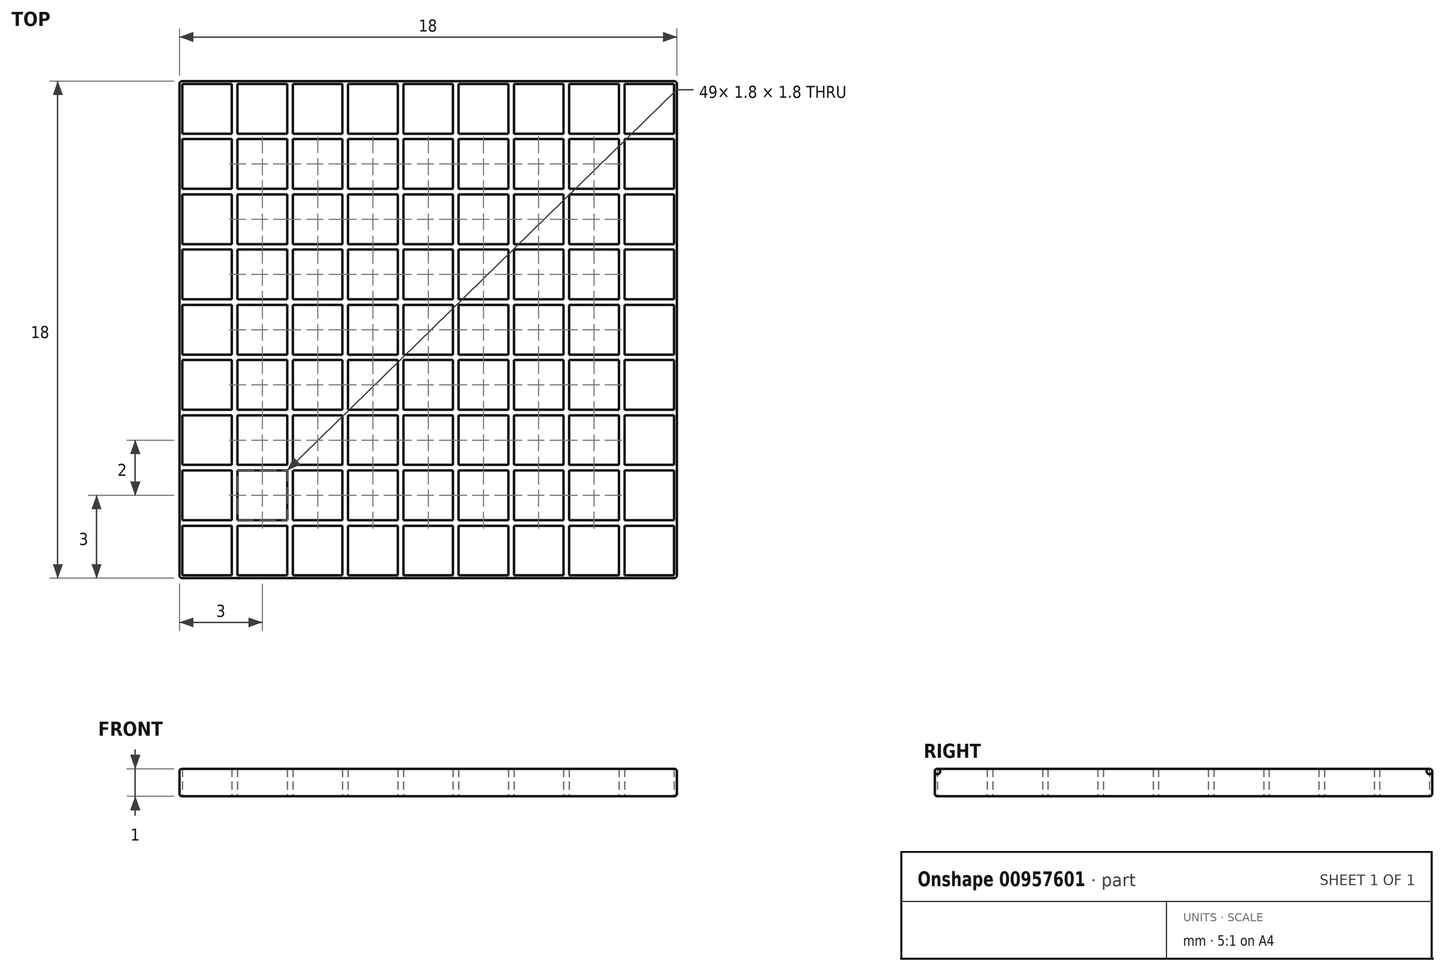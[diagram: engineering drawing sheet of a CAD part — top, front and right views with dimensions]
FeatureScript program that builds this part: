
annotation { "Feature Type Name" : "Feature", "Feature Type Description" : "" }
export const myFeature = defineFeature(function(context is Context, id is Id, definition is map)
    precondition{}
    {
        {
            var Q0;
            Q0=qCreatedBy(makeId("Top.planeOp"),FACE);
            var sketch = newSketch(context, id + "F0", { "sketchPlane" : qUnion([Q0])});
            skLineSegment(sketch, "E0.bottom", {"start": v(-9, 9) * mm, "end": v(9, 9) * mm});
            skLineSegment(sketch, "E0.top", {"start": v(-9, -9) * mm, "end": v(9, -9) * mm});
            skLineSegment(sketch, "E0.left", {"start": v(-9, 9) * mm, "end": v(-9, -9) * mm});
            skLineSegment(sketch, "E0.right", {"start": v(9, 9) * mm, "end": v(9, -9) * mm});
            skPoint(sketch, "E0.middle", {"position": v(0, 0) * mm});
            skLineSegment(sketch, "E1", {"start": v(-8.9, 9) * mm, "end": v(-8.9, -9) * mm});
            skLineSegment(sketch, "E2", {"start": v(-7.1, 9) * mm, "end": v(-7.1, -9) * mm});
            skLineSegment(sketch, "E3", {"start": v(-6.9, 9) * mm, "end": v(-6.9, -9) * mm});
            skLineSegment(sketch, "E4", {"start": v(-5.1, 9) * mm, "end": v(-5.1, -9) * mm});
            skLineSegment(sketch, "E5", {"start": v(-4.9, 9) * mm, "end": v(-4.9, -9) * mm});
            skLineSegment(sketch, "E6", {"start": v(-3.1, 9) * mm, "end": v(-3.1, -9) * mm});
            skLineSegment(sketch, "E7", {"start": v(-2.9, 9) * mm, "end": v(-2.9, -9) * mm});
            skLineSegment(sketch, "E8", {"start": v(-1.1, 9) * mm, "end": v(-1.1, -9) * mm});
            skLineSegment(sketch, "E9", {"start": v(-0.9, 9) * mm, "end": v(-0.9, -9) * mm});
            skLineSegment(sketch, "E10", {"start": v(0.9, 9) * mm, "end": v(0.9, -9) * mm});
            skLineSegment(sketch, "E11", {"start": v(1.1, 9) * mm, "end": v(1.1, -9) * mm});
            skLineSegment(sketch, "E12", {"start": v(2.9, 9) * mm, "end": v(2.9, -9) * mm});
            skLineSegment(sketch, "E13", {"start": v(3.1, 9) * mm, "end": v(3.1, -9) * mm});
            skLineSegment(sketch, "E14", {"start": v(4.9, 9) * mm, "end": v(4.9, -9) * mm});
            skLineSegment(sketch, "E15", {"start": v(5.1, 9) * mm, "end": v(5.1, -9) * mm});
            skLineSegment(sketch, "E16", {"start": v(6.9, 9) * mm, "end": v(6.9, -9) * mm});
            skLineSegment(sketch, "E17", {"start": v(7.1, 9) * mm, "end": v(7.1, -9) * mm});
            skLineSegment(sketch, "E18", {"start": v(8.9, 9) * mm, "end": v(8.9, -9) * mm});
            skLineSegment(sketch, "E19", {"start": v(9, 8.9) * mm, "end": v(-9, 8.9) * mm});
            skLineSegment(sketch, "E20", {"start": v(9, 7.1) * mm, "end": v(-9, 7.1) * mm});
            skLineSegment(sketch, "E21", {"start": v(9, 6.9) * mm, "end": v(-9, 6.9) * mm});
            skLineSegment(sketch, "E22", {"start": v(9, 5.1) * mm, "end": v(-9, 5.1) * mm});
            skLineSegment(sketch, "E23", {"start": v(9, 4.9) * mm, "end": v(-9, 4.9) * mm});
            skLineSegment(sketch, "E24", {"start": v(9, 3.1) * mm, "end": v(-9, 3.1) * mm});
            skLineSegment(sketch, "E25", {"start": v(9, 2.9) * mm, "end": v(-9, 2.9) * mm});
            skLineSegment(sketch, "E26", {"start": v(9, 1.1) * mm, "end": v(-9, 1.1) * mm});
            skLineSegment(sketch, "E27", {"start": v(9, 0.9) * mm, "end": v(-9, 0.9) * mm});
            skLineSegment(sketch, "E28", {"start": v(9, -0.9) * mm, "end": v(-9, -0.9) * mm});
            skLineSegment(sketch, "E29", {"start": v(9, -1.1) * mm, "end": v(-9, -1.1) * mm});
            skLineSegment(sketch, "E30", {"start": v(9, -2.9) * mm, "end": v(-9, -2.9) * mm});
            skLineSegment(sketch, "E31", {"start": v(9, -3.1) * mm, "end": v(-9, -3.1) * mm});
            skLineSegment(sketch, "E32", {"start": v(9, -4.9) * mm, "end": v(-9, -4.9) * mm});
            skLineSegment(sketch, "E33", {"start": v(9, -5.1) * mm, "end": v(-9, -5.1) * mm});
            skLineSegment(sketch, "E34", {"start": v(9, -6.9) * mm, "end": v(-9, -6.9) * mm});
            skLineSegment(sketch, "E35", {"start": v(9, -7.1) * mm, "end": v(-9, -7.1) * mm});
            skLineSegment(sketch, "E36", {"start": v(9, -8.9) * mm, "end": v(-9, -8.9) * mm});
            skSolve(sketch);
        }
        {
            var Q0;
            {var subQ0=sQuery(id+"F0.wireOp",EDGE,"E30");var subQ1=sQuery(id+"F0.wireOp",EDGE,"E10");var subQ2=makeQuery(id+"F0.imprint","INTERSECT",VERTEX,{"derivedFrom":[subQ1,subQ0]});Q0=makeQuery(id+"F0.imprint","IMPRINT",FACE,{"disambiguationData":[TD([[makeQuery(id+"F0.imprint","IMPRINT",EDGE,{"disambiguationData":[TD([[subQ2,-1.0]])],"derivedFrom":subQ1}),1.0]])]});}
            var Q1;
            {var subQ0=sQuery(id+"F0.wireOp",EDGE,"E26");var subQ1=sQuery(id+"F0.wireOp",EDGE,"E11");var subQ2=makeQuery(id+"F0.imprint","INTERSECT",VERTEX,{"derivedFrom":[subQ1,subQ0]});Q1=makeQuery(id+"F0.imprint","IMPRINT",FACE,{"disambiguationData":[TD([[makeQuery(id+"F0.imprint","IMPRINT",EDGE,{"disambiguationData":[TD([[subQ2,-1.0]])],"derivedFrom":subQ1}),1.0]])]});}
            var Q2;
            {var subQ0=sQuery(id+"F0.wireOp",EDGE,"E25");var subQ1=sQuery(id+"F0.wireOp",EDGE,"E8");var subQ2=makeQuery(id+"F0.imprint","INTERSECT",VERTEX,{"derivedFrom":[subQ1,subQ0]});Q2=makeQuery(id+"F0.imprint","IMPRINT",FACE,{"disambiguationData":[TD([[makeQuery(id+"F0.imprint","IMPRINT",EDGE,{"disambiguationData":[TD([[subQ2,-1.0]])],"derivedFrom":subQ1}),1.0]])]});}
            var Q3;
            {var subQ0=sQuery(id+"F0.wireOp",EDGE,"E24");var subQ1=sQuery(id+"F0.wireOp",EDGE,"E10");var subQ2=makeQuery(id+"F0.imprint","INTERSECT",VERTEX,{"derivedFrom":[subQ1,subQ0]});Q3=makeQuery(id+"F0.imprint","IMPRINT",FACE,{"disambiguationData":[TD([[makeQuery(id+"F0.imprint","IMPRINT",EDGE,{"disambiguationData":[TD([[subQ2,-1.0]])],"derivedFrom":subQ1}),1.0]])]});}
            var Q4;
            {var subQ0=sQuery(id+"F0.wireOp",EDGE,"E30");var subQ1=sQuery(id+"F0.wireOp",EDGE,"E15");var subQ2=makeQuery(id+"F0.imprint","INTERSECT",VERTEX,{"derivedFrom":[subQ1,subQ0]});Q4=makeQuery(id+"F0.imprint","IMPRINT",FACE,{"disambiguationData":[TD([[makeQuery(id+"F0.imprint","IMPRINT",EDGE,{"disambiguationData":[TD([[subQ2,-1.0]])],"derivedFrom":subQ1}),1.0]])]});}
            var Q5;
            {var subQ0=sQuery(id+"F0.wireOp",EDGE,"E35");var subQ1=sQuery(id+"F0.wireOp",EDGE,"E12");var subQ2=makeQuery(id+"F0.imprint","INTERSECT",VERTEX,{"derivedFrom":[subQ1,subQ0]});Q5=makeQuery(id+"F0.imprint","IMPRINT",FACE,{"disambiguationData":[TD([[makeQuery(id+"F0.imprint","IMPRINT",EDGE,{"disambiguationData":[TD([[subQ2,-1.0]])],"derivedFrom":subQ1}),1.0]])]});}
            var Q6;
            {var subQ0=sQuery(id+"F0.wireOp",EDGE,"E35");var subQ1=sQuery(id+"F0.wireOp",EDGE,"E14");var subQ2=makeQuery(id+"F0.imprint","INTERSECT",VERTEX,{"derivedFrom":[subQ1,subQ0]});Q6=makeQuery(id+"F0.imprint","IMPRINT",FACE,{"disambiguationData":[TD([[makeQuery(id+"F0.imprint","IMPRINT",EDGE,{"disambiguationData":[TD([[subQ2,-1.0]])],"derivedFrom":subQ1}),1.0]])]});}
            var Q7;
            {var subQ0=sQuery(id+"F0.wireOp",EDGE,"E32");var subQ1=sQuery(id+"F0.wireOp",EDGE,"E10");var subQ2=makeQuery(id+"F0.imprint","INTERSECT",VERTEX,{"derivedFrom":[subQ1,subQ0]});Q7=makeQuery(id+"F0.imprint","IMPRINT",FACE,{"disambiguationData":[TD([[makeQuery(id+"F0.imprint","IMPRINT",EDGE,{"disambiguationData":[TD([[subQ2,-1.0]])],"derivedFrom":subQ1}),1.0]])]});}
            var Q8;
            {var subQ0=sQuery(id+"F0.wireOp",EDGE,"E23");var subQ1=sQuery(id+"F0.wireOp",EDGE,"E14");var subQ2=makeQuery(id+"F0.imprint","INTERSECT",VERTEX,{"derivedFrom":[subQ1,subQ0]});Q8=makeQuery(id+"F0.imprint","IMPRINT",FACE,{"disambiguationData":[TD([[makeQuery(id+"F0.imprint","IMPRINT",EDGE,{"disambiguationData":[TD([[subQ2,-1.0]])],"derivedFrom":subQ1}),1.0]])]});}
            var Q9;
            {var subQ0=sQuery(id+"F0.wireOp",EDGE,"E23");var subQ1=sQuery(id+"F0.wireOp",EDGE,"E16");var subQ2=makeQuery(id+"F0.imprint","INTERSECT",VERTEX,{"derivedFrom":[subQ1,subQ0]});Q9=makeQuery(id+"F0.imprint","IMPRINT",FACE,{"disambiguationData":[TD([[makeQuery(id+"F0.imprint","IMPRINT",EDGE,{"disambiguationData":[TD([[subQ2,-1.0]])],"derivedFrom":subQ1}),1.0]])]});}
            var Q10;
            {var subQ0=sQuery(id+"F0.wireOp",EDGE,"E22");var subQ1=sQuery(id+"F0.wireOp",EDGE,"E9");var subQ2=makeQuery(id+"F0.imprint","INTERSECT",VERTEX,{"derivedFrom":[subQ1,subQ0]});Q10=makeQuery(id+"F0.imprint","IMPRINT",FACE,{"disambiguationData":[TD([[makeQuery(id+"F0.imprint","IMPRINT",EDGE,{"disambiguationData":[TD([[subQ2,-1.0]])],"derivedFrom":subQ1}),1.0]])]});}
            var Q11;
            {var subQ0=sQuery(id+"F0.wireOp",EDGE,"E27");var subQ1=sQuery(id+"F0.wireOp",EDGE,"E10");var subQ2=makeQuery(id+"F0.imprint","INTERSECT",VERTEX,{"derivedFrom":[subQ1,subQ0]});Q11=makeQuery(id+"F0.imprint","IMPRINT",FACE,{"disambiguationData":[TD([[makeQuery(id+"F0.imprint","IMPRINT",EDGE,{"disambiguationData":[TD([[subQ2,-1.0]])],"derivedFrom":subQ1}),1.0]])]});}
            var Q12;
            {var subQ0=sQuery(id+"F0.wireOp",EDGE,"E31");var subQ1=sQuery(id+"F0.wireOp",EDGE,"E2");var subQ2=makeQuery(id+"F0.imprint","INTERSECT",VERTEX,{"derivedFrom":[subQ1,subQ0]});Q12=makeQuery(id+"F0.imprint","IMPRINT",FACE,{"disambiguationData":[TD([[makeQuery(id+"F0.imprint","IMPRINT",EDGE,{"disambiguationData":[TD([[subQ2,-1.0]])],"derivedFrom":subQ1}),1.0]])]});}
            var Q13;
            {var subQ0=sQuery(id+"F0.wireOp",EDGE,"E30");var subQ1=sQuery(id+"F0.wireOp",EDGE,"E13");var subQ2=makeQuery(id+"F0.imprint","INTERSECT",VERTEX,{"derivedFrom":[subQ1,subQ0]});Q13=makeQuery(id+"F0.imprint","IMPRINT",FACE,{"disambiguationData":[TD([[makeQuery(id+"F0.imprint","IMPRINT",EDGE,{"disambiguationData":[TD([[subQ2,-1.0]])],"derivedFrom":subQ1}),1.0]])]});}
            var Q14;
            {var subQ0=sQuery(id+"F0.wireOp",EDGE,"E33");var subQ1=sQuery(id+"F0.wireOp",EDGE,"E16");var subQ2=makeQuery(id+"F0.imprint","INTERSECT",VERTEX,{"derivedFrom":[subQ1,subQ0]});Q14=makeQuery(id+"F0.imprint","IMPRINT",FACE,{"disambiguationData":[TD([[makeQuery(id+"F0.imprint","IMPRINT",EDGE,{"disambiguationData":[TD([[subQ2,-1.0]])],"derivedFrom":subQ1}),1.0]])]});}
            var Q15;
            {var subQ0=sQuery(id+"F0.wireOp",EDGE,"E29");var subQ1=sQuery(id+"F0.wireOp",EDGE,"E8");var subQ2=makeQuery(id+"F0.imprint","INTERSECT",VERTEX,{"derivedFrom":[subQ1,subQ0]});Q15=makeQuery(id+"F0.imprint","IMPRINT",FACE,{"disambiguationData":[TD([[makeQuery(id+"F0.imprint","IMPRINT",EDGE,{"disambiguationData":[TD([[subQ2,-1.0]])],"derivedFrom":subQ1}),1.0]])]});}
            var Q16;
            {var subQ0=sQuery(id+"F0.wireOp",EDGE,"E26");var subQ1=sQuery(id+"F0.wireOp",EDGE,"E1");var subQ2=makeQuery(id+"F0.imprint","INTERSECT",VERTEX,{"derivedFrom":[subQ1,subQ0]});Q16=makeQuery(id+"F0.imprint","IMPRINT",FACE,{"disambiguationData":[TD([[makeQuery(id+"F0.imprint","IMPRINT",EDGE,{"disambiguationData":[TD([[subQ2,-1.0]])],"derivedFrom":subQ1}),1.0]])]});}
            var Q17;
            {var subQ0=sQuery(id+"F0.wireOp",EDGE,"E30");var subQ1=sQuery(id+"F0.wireOp",EDGE,"E12");var subQ2=makeQuery(id+"F0.imprint","INTERSECT",VERTEX,{"derivedFrom":[subQ1,subQ0]});Q17=makeQuery(id+"F0.imprint","IMPRINT",FACE,{"disambiguationData":[TD([[makeQuery(id+"F0.imprint","IMPRINT",EDGE,{"disambiguationData":[TD([[subQ2,-1.0]])],"derivedFrom":subQ1}),1.0]])]});}
            var Q18;
            {var subQ0=sQuery(id+"F0.wireOp",EDGE,"E29");var subQ1=sQuery(id+"F0.wireOp",EDGE,"E12");var subQ2=makeQuery(id+"F0.imprint","INTERSECT",VERTEX,{"derivedFrom":[subQ1,subQ0]});Q18=makeQuery(id+"F0.imprint","IMPRINT",FACE,{"disambiguationData":[TD([[makeQuery(id+"F0.imprint","IMPRINT",EDGE,{"disambiguationData":[TD([[subQ2,-1.0]])],"derivedFrom":subQ1}),1.0]])]});}
            var Q19;
            {var subQ0=sQuery(id+"F0.wireOp",EDGE,"E31");var subQ1=sQuery(id+"F0.wireOp",EDGE,"E6");var subQ2=makeQuery(id+"F0.imprint","INTERSECT",VERTEX,{"derivedFrom":[subQ1,subQ0]});Q19=makeQuery(id+"F0.imprint","IMPRINT",FACE,{"disambiguationData":[TD([[makeQuery(id+"F0.imprint","IMPRINT",EDGE,{"disambiguationData":[TD([[subQ2,-1.0]])],"derivedFrom":subQ1}),1.0]])]});}
            var Q20;
            {var subQ0=sQuery(id+"F0.wireOp",EDGE,"E29");var subQ1=sQuery(id+"F0.wireOp",EDGE,"E10");var subQ2=makeQuery(id+"F0.imprint","INTERSECT",VERTEX,{"derivedFrom":[subQ1,subQ0]});Q20=makeQuery(id+"F0.imprint","IMPRINT",FACE,{"disambiguationData":[TD([[makeQuery(id+"F0.imprint","IMPRINT",EDGE,{"disambiguationData":[TD([[subQ2,-1.0]])],"derivedFrom":subQ1}),1.0]])]});}
            var Q21;
            {var subQ0=sQuery(id+"F0.wireOp",EDGE,"E25");var subQ1=sQuery(id+"F0.wireOp",EDGE,"E16");var subQ2=makeQuery(id+"F0.imprint","INTERSECT",VERTEX,{"derivedFrom":[subQ1,subQ0]});Q21=makeQuery(id+"F0.imprint","IMPRINT",FACE,{"disambiguationData":[TD([[makeQuery(id+"F0.imprint","IMPRINT",EDGE,{"disambiguationData":[TD([[subQ2,-1.0]])],"derivedFrom":subQ1}),1.0]])]});}
            var Q22;
            {var subQ0=sQuery(id+"F0.wireOp",EDGE,"E35");var subQ1=sQuery(id+"F0.wireOp",EDGE,"E16");var subQ2=makeQuery(id+"F0.imprint","INTERSECT",VERTEX,{"derivedFrom":[subQ1,subQ0]});Q22=makeQuery(id+"F0.imprint","IMPRINT",FACE,{"disambiguationData":[TD([[makeQuery(id+"F0.imprint","IMPRINT",EDGE,{"disambiguationData":[TD([[subQ2,-1.0]])],"derivedFrom":subQ1}),1.0]])]});}
            var Q23;
            {var subQ0=sQuery(id+"F0.wireOp",EDGE,"E31");var subQ1=sQuery(id+"F0.wireOp",EDGE,"E12");var subQ2=makeQuery(id+"F0.imprint","INTERSECT",VERTEX,{"derivedFrom":[subQ1,subQ0]});Q23=makeQuery(id+"F0.imprint","IMPRINT",FACE,{"disambiguationData":[TD([[makeQuery(id+"F0.imprint","IMPRINT",EDGE,{"disambiguationData":[TD([[subQ2,-1.0]])],"derivedFrom":subQ1}),1.0]])]});}
            var Q24;
            {var subQ0=sQuery(id+"F0.wireOp",EDGE,"E24");var subQ1=sQuery(id+"F0.wireOp",EDGE,"E1");var subQ2=makeQuery(id+"F0.imprint","INTERSECT",VERTEX,{"derivedFrom":[subQ1,subQ0]});Q24=makeQuery(id+"F0.imprint","IMPRINT",FACE,{"disambiguationData":[TD([[makeQuery(id+"F0.imprint","IMPRINT",EDGE,{"disambiguationData":[TD([[subQ2,-1.0]])],"derivedFrom":subQ1}),1.0]])]});}
            var Q25;
            {var subQ0=sQuery(id+"F0.wireOp",EDGE,"E27");var subQ1=sQuery(id+"F0.wireOp",EDGE,"E16");var subQ2=makeQuery(id+"F0.imprint","INTERSECT",VERTEX,{"derivedFrom":[subQ1,subQ0]});Q25=makeQuery(id+"F0.imprint","IMPRINT",FACE,{"disambiguationData":[TD([[makeQuery(id+"F0.imprint","IMPRINT",EDGE,{"disambiguationData":[TD([[subQ2,-1.0]])],"derivedFrom":subQ1}),1.0]])]});}
            var Q26;
            {var subQ0=sQuery(id+"F0.wireOp",EDGE,"E26");var subQ1=sQuery(id+"F0.wireOp",EDGE,"E9");var subQ2=makeQuery(id+"F0.imprint","INTERSECT",VERTEX,{"derivedFrom":[subQ1,subQ0]});Q26=makeQuery(id+"F0.imprint","IMPRINT",FACE,{"disambiguationData":[TD([[makeQuery(id+"F0.imprint","IMPRINT",EDGE,{"disambiguationData":[TD([[subQ2,-1.0]])],"derivedFrom":subQ1}),1.0]])]});}
            var Q27;
            {var subQ0=sQuery(id+"F0.wireOp",EDGE,"E35");var subQ1=sQuery(id+"F0.wireOp",EDGE,"E2");var subQ2=makeQuery(id+"F0.imprint","INTERSECT",VERTEX,{"derivedFrom":[subQ1,subQ0]});Q27=makeQuery(id+"F0.imprint","IMPRINT",FACE,{"disambiguationData":[TD([[makeQuery(id+"F0.imprint","IMPRINT",EDGE,{"disambiguationData":[TD([[subQ2,-1.0]])],"derivedFrom":subQ1}),1.0]])]});}
            var Q28;
            {var subQ0=sQuery(id+"F0.wireOp",EDGE,"E22");var subQ1=sQuery(id+"F0.wireOp",EDGE,"E16");var subQ2=makeQuery(id+"F0.imprint","INTERSECT",VERTEX,{"derivedFrom":[subQ1,subQ0]});Q28=makeQuery(id+"F0.imprint","IMPRINT",FACE,{"disambiguationData":[TD([[makeQuery(id+"F0.imprint","IMPRINT",EDGE,{"disambiguationData":[TD([[subQ2,-1.0]])],"derivedFrom":subQ1}),1.0]])]});}
            var Q29;
            {var subQ0=sQuery(id+"F0.wireOp",EDGE,"E35");var subQ1=sQuery(id+"F0.wireOp",EDGE,"E8");var subQ2=makeQuery(id+"F0.imprint","INTERSECT",VERTEX,{"derivedFrom":[subQ1,subQ0]});Q29=makeQuery(id+"F0.imprint","IMPRINT",FACE,{"disambiguationData":[TD([[makeQuery(id+"F0.imprint","IMPRINT",EDGE,{"disambiguationData":[TD([[subQ2,-1.0]])],"derivedFrom":subQ1}),1.0]])]});}
            var Q30;
            {var subQ0=sQuery(id+"F0.wireOp",EDGE,"E24");var subQ1=sQuery(id+"F0.wireOp",EDGE,"E7");var subQ2=makeQuery(id+"F0.imprint","INTERSECT",VERTEX,{"derivedFrom":[subQ1,subQ0]});Q30=makeQuery(id+"F0.imprint","IMPRINT",FACE,{"disambiguationData":[TD([[makeQuery(id+"F0.imprint","IMPRINT",EDGE,{"disambiguationData":[TD([[subQ2,-1.0]])],"derivedFrom":subQ1}),1.0]])]});}
            var Q31;
            {var subQ0=sQuery(id+"F0.wireOp",EDGE,"E21");var subQ1=sQuery(id+"F0.wireOp",EDGE,"E16");var subQ2=makeQuery(id+"F0.imprint","INTERSECT",VERTEX,{"derivedFrom":[subQ1,subQ0]});Q31=makeQuery(id+"F0.imprint","IMPRINT",FACE,{"disambiguationData":[TD([[makeQuery(id+"F0.imprint","IMPRINT",EDGE,{"disambiguationData":[TD([[subQ2,-1.0]])],"derivedFrom":subQ1}),1.0]])]});}
            var Q32;
            {var subQ0=sQuery(id+"F0.wireOp",EDGE,"E32");var subQ1=sQuery(id+"F0.wireOp",EDGE,"E11");var subQ2=makeQuery(id+"F0.imprint","INTERSECT",VERTEX,{"derivedFrom":[subQ1,subQ0]});Q32=makeQuery(id+"F0.imprint","IMPRINT",FACE,{"disambiguationData":[TD([[makeQuery(id+"F0.imprint","IMPRINT",EDGE,{"disambiguationData":[TD([[subQ2,-1.0]])],"derivedFrom":subQ1}),1.0]])]});}
            var Q33;
            {var subQ0=sQuery(id+"F0.wireOp",EDGE,"E33");var subQ1=sQuery(id+"F0.wireOp",EDGE,"E8");var subQ2=makeQuery(id+"F0.imprint","INTERSECT",VERTEX,{"derivedFrom":[subQ1,subQ0]});Q33=makeQuery(id+"F0.imprint","IMPRINT",FACE,{"disambiguationData":[TD([[makeQuery(id+"F0.imprint","IMPRINT",EDGE,{"disambiguationData":[TD([[subQ2,-1.0]])],"derivedFrom":subQ1}),1.0]])]});}
            var Q34;
            {var subQ0=sQuery(id+"F0.wireOp",EDGE,"E30");var subQ1=sQuery(id+"F0.wireOp",EDGE,"E9");var subQ2=makeQuery(id+"F0.imprint","INTERSECT",VERTEX,{"derivedFrom":[subQ1,subQ0]});Q34=makeQuery(id+"F0.imprint","IMPRINT",FACE,{"disambiguationData":[TD([[makeQuery(id+"F0.imprint","IMPRINT",EDGE,{"disambiguationData":[TD([[subQ2,-1.0]])],"derivedFrom":subQ1}),1.0]])]});}
            var Q35;
            {var subQ0=sQuery(id+"F0.wireOp",EDGE,"E22");var subQ1=sQuery(id+"F0.wireOp",EDGE,"E8");var subQ2=makeQuery(id+"F0.imprint","INTERSECT",VERTEX,{"derivedFrom":[subQ1,subQ0]});Q35=makeQuery(id+"F0.imprint","IMPRINT",FACE,{"disambiguationData":[TD([[makeQuery(id+"F0.imprint","IMPRINT",EDGE,{"disambiguationData":[TD([[subQ2,-1.0]])],"derivedFrom":subQ1}),1.0]])]});}
            var Q36;
            {var subQ0=sQuery(id+"F0.wireOp",EDGE,"E27");var subQ1=sQuery(id+"F0.wireOp",EDGE,"E2");var subQ2=makeQuery(id+"F0.imprint","INTERSECT",VERTEX,{"derivedFrom":[subQ1,subQ0]});Q36=makeQuery(id+"F0.imprint","IMPRINT",FACE,{"disambiguationData":[TD([[makeQuery(id+"F0.imprint","IMPRINT",EDGE,{"disambiguationData":[TD([[subQ2,-1.0]])],"derivedFrom":subQ1}),1.0]])]});}
            var Q37;
            {var subQ0=sQuery(id+"F0.wireOp",EDGE,"E30");var subQ1=sQuery(id+"F0.wireOp",EDGE,"E11");var subQ2=makeQuery(id+"F0.imprint","INTERSECT",VERTEX,{"derivedFrom":[subQ1,subQ0]});Q37=makeQuery(id+"F0.imprint","IMPRINT",FACE,{"disambiguationData":[TD([[makeQuery(id+"F0.imprint","IMPRINT",EDGE,{"disambiguationData":[TD([[subQ2,-1.0]])],"derivedFrom":subQ1}),1.0]])]});}
            var Q38;
            {var subQ0=sQuery(id+"F0.wireOp",EDGE,"E26");var subQ1=sQuery(id+"F0.wireOp",EDGE,"E5");var subQ2=makeQuery(id+"F0.imprint","INTERSECT",VERTEX,{"derivedFrom":[subQ1,subQ0]});Q38=makeQuery(id+"F0.imprint","IMPRINT",FACE,{"disambiguationData":[TD([[makeQuery(id+"F0.imprint","IMPRINT",EDGE,{"disambiguationData":[TD([[subQ2,-1.0]])],"derivedFrom":subQ1}),1.0]])]});}
            var Q39;
            {var subQ0=sQuery(id+"F0.wireOp",EDGE,"E31");var subQ1=sQuery(id+"F0.wireOp",EDGE,"E8");var subQ2=makeQuery(id+"F0.imprint","INTERSECT",VERTEX,{"derivedFrom":[subQ1,subQ0]});Q39=makeQuery(id+"F0.imprint","IMPRINT",FACE,{"disambiguationData":[TD([[makeQuery(id+"F0.imprint","IMPRINT",EDGE,{"disambiguationData":[TD([[subQ2,-1.0]])],"derivedFrom":subQ1}),1.0]])]});}
            var Q40;
            {var subQ0=sQuery(id+"F0.wireOp",EDGE,"E32");var subQ1=sQuery(id+"F0.wireOp",EDGE,"E7");var subQ2=makeQuery(id+"F0.imprint","INTERSECT",VERTEX,{"derivedFrom":[subQ1,subQ0]});Q40=makeQuery(id+"F0.imprint","IMPRINT",FACE,{"disambiguationData":[TD([[makeQuery(id+"F0.imprint","IMPRINT",EDGE,{"disambiguationData":[TD([[subQ2,-1.0]])],"derivedFrom":subQ1}),1.0]])]});}
            var Q41;
            {var subQ0=sQuery(id+"F0.wireOp",EDGE,"E24");var subQ1=sQuery(id+"F0.wireOp",EDGE,"E17");var subQ2=makeQuery(id+"F0.imprint","INTERSECT",VERTEX,{"derivedFrom":[subQ1,subQ0]});Q41=makeQuery(id+"F0.imprint","IMPRINT",FACE,{"disambiguationData":[TD([[makeQuery(id+"F0.imprint","IMPRINT",EDGE,{"disambiguationData":[TD([[subQ2,-1.0]])],"derivedFrom":subQ1}),1.0]])]});}
            var Q42;
            {var subQ0=sQuery(id+"F0.wireOp",EDGE,"E26");var subQ1=sQuery(id+"F0.wireOp",EDGE,"E14");var subQ2=makeQuery(id+"F0.imprint","INTERSECT",VERTEX,{"derivedFrom":[subQ1,subQ0]});Q42=makeQuery(id+"F0.imprint","IMPRINT",FACE,{"disambiguationData":[TD([[makeQuery(id+"F0.imprint","IMPRINT",EDGE,{"disambiguationData":[TD([[subQ2,-1.0]])],"derivedFrom":subQ1}),1.0]])]});}
            var Q43;
            {var subQ0=sQuery(id+"F0.wireOp",EDGE,"E31");var subQ1=sQuery(id+"F0.wireOp",EDGE,"E14");var subQ2=makeQuery(id+"F0.imprint","INTERSECT",VERTEX,{"derivedFrom":[subQ1,subQ0]});Q43=makeQuery(id+"F0.imprint","IMPRINT",FACE,{"disambiguationData":[TD([[makeQuery(id+"F0.imprint","IMPRINT",EDGE,{"disambiguationData":[TD([[subQ2,-1.0]])],"derivedFrom":subQ1}),1.0]])]});}
            var Q44;
            {var subQ0=sQuery(id+"F0.wireOp",EDGE,"E24");var subQ1=sQuery(id+"F0.wireOp",EDGE,"E5");var subQ2=makeQuery(id+"F0.imprint","INTERSECT",VERTEX,{"derivedFrom":[subQ1,subQ0]});Q44=makeQuery(id+"F0.imprint","IMPRINT",FACE,{"disambiguationData":[TD([[makeQuery(id+"F0.imprint","IMPRINT",EDGE,{"disambiguationData":[TD([[subQ2,-1.0]])],"derivedFrom":subQ1}),1.0]])]});}
            var Q45;
            {var subQ0=sQuery(id+"F0.wireOp",EDGE,"E26");var subQ1=sQuery(id+"F0.wireOp",EDGE,"E12");var subQ2=makeQuery(id+"F0.imprint","INTERSECT",VERTEX,{"derivedFrom":[subQ1,subQ0]});Q45=makeQuery(id+"F0.imprint","IMPRINT",FACE,{"disambiguationData":[TD([[makeQuery(id+"F0.imprint","IMPRINT",EDGE,{"disambiguationData":[TD([[subQ2,-1.0]])],"derivedFrom":subQ1}),1.0]])]});}
            var Q46;
            {var subQ0=sQuery(id+"F0.wireOp",EDGE,"E30");var subQ1=sQuery(id+"F0.wireOp",EDGE,"E5");var subQ2=makeQuery(id+"F0.imprint","INTERSECT",VERTEX,{"derivedFrom":[subQ1,subQ0]});Q46=makeQuery(id+"F0.imprint","IMPRINT",FACE,{"disambiguationData":[TD([[makeQuery(id+"F0.imprint","IMPRINT",EDGE,{"disambiguationData":[TD([[subQ2,-1.0]])],"derivedFrom":subQ1}),1.0]])]});}
            var Q47;
            {var subQ0=sQuery(id+"F0.wireOp",EDGE,"E33");var subQ1=sQuery(id+"F0.wireOp",EDGE,"E14");var subQ2=makeQuery(id+"F0.imprint","INTERSECT",VERTEX,{"derivedFrom":[subQ1,subQ0]});Q47=makeQuery(id+"F0.imprint","IMPRINT",FACE,{"disambiguationData":[TD([[makeQuery(id+"F0.imprint","IMPRINT",EDGE,{"disambiguationData":[TD([[subQ2,-1.0]])],"derivedFrom":subQ1}),1.0]])]});}
            var Q48;
            {var subQ0=sQuery(id+"F0.wireOp",EDGE,"E32");var subQ1=sQuery(id+"F0.wireOp",EDGE,"E9");var subQ2=makeQuery(id+"F0.imprint","INTERSECT",VERTEX,{"derivedFrom":[subQ1,subQ0]});Q48=makeQuery(id+"F0.imprint","IMPRINT",FACE,{"disambiguationData":[TD([[makeQuery(id+"F0.imprint","IMPRINT",EDGE,{"disambiguationData":[TD([[subQ2,-1.0]])],"derivedFrom":subQ1}),1.0]])]});}
            var Q49;
            {var subQ0=sQuery(id+"F0.wireOp",EDGE,"E25");var subQ1=sQuery(id+"F0.wireOp",EDGE,"E6");var subQ2=makeQuery(id+"F0.imprint","INTERSECT",VERTEX,{"derivedFrom":[subQ1,subQ0]});Q49=makeQuery(id+"F0.imprint","IMPRINT",FACE,{"disambiguationData":[TD([[makeQuery(id+"F0.imprint","IMPRINT",EDGE,{"disambiguationData":[TD([[subQ2,-1.0]])],"derivedFrom":subQ1}),1.0]])]});}
            var Q50;
            {var subQ0=sQuery(id+"F0.wireOp",EDGE,"E19");var subQ1=sQuery(id+"F0.wireOp",EDGE,"E16");var subQ2=makeQuery(id+"F0.imprint","INTERSECT",VERTEX,{"derivedFrom":[subQ1,subQ0]});Q50=makeQuery(id+"F0.imprint","IMPRINT",FACE,{"disambiguationData":[TD([[makeQuery(id+"F0.imprint","IMPRINT",EDGE,{"disambiguationData":[TD([[subQ2,-1.0]])],"derivedFrom":subQ1}),1.0]])]});}
            var Q51;
            {var subQ0=sQuery(id+"F0.wireOp",EDGE,"E19");var subQ1=sQuery(id+"F0.wireOp",EDGE,"E10");var subQ2=makeQuery(id+"F0.imprint","INTERSECT",VERTEX,{"derivedFrom":[subQ1,subQ0]});Q51=makeQuery(id+"F0.imprint","IMPRINT",FACE,{"disambiguationData":[TD([[makeQuery(id+"F0.imprint","IMPRINT",EDGE,{"disambiguationData":[TD([[subQ2,-1.0]])],"derivedFrom":subQ1}),1.0]])]});}
            var Q52;
            {var subQ0=sQuery(id+"F0.wireOp",EDGE,"E19");var subQ1=sQuery(id+"F0.wireOp",EDGE,"E2");var subQ2=makeQuery(id+"F0.imprint","INTERSECT",VERTEX,{"derivedFrom":[subQ1,subQ0]});Q52=makeQuery(id+"F0.imprint","IMPRINT",FACE,{"disambiguationData":[TD([[makeQuery(id+"F0.imprint","IMPRINT",EDGE,{"disambiguationData":[TD([[subQ2,-1.0]])],"derivedFrom":subQ1}),1.0]])]});}
            var Q53;
            {var subQ0=sQuery(id+"F0.wireOp",EDGE,"E32");var subQ1=sQuery(id+"F0.wireOp",EDGE,"E17");var subQ2=makeQuery(id+"F0.imprint","INTERSECT",VERTEX,{"derivedFrom":[subQ1,subQ0]});Q53=makeQuery(id+"F0.imprint","IMPRINT",FACE,{"disambiguationData":[TD([[makeQuery(id+"F0.imprint","IMPRINT",EDGE,{"disambiguationData":[TD([[subQ2,-1.0]])],"derivedFrom":subQ1}),1.0]])]});}
            var Q54;
            {var subQ0=sQuery(id+"F0.wireOp",EDGE,"E30");var subQ1=sQuery(id+"F0.wireOp",EDGE,"E17");var subQ2=makeQuery(id+"F0.imprint","INTERSECT",VERTEX,{"derivedFrom":[subQ1,subQ0]});Q54=makeQuery(id+"F0.imprint","IMPRINT",FACE,{"disambiguationData":[TD([[makeQuery(id+"F0.imprint","IMPRINT",EDGE,{"disambiguationData":[TD([[subQ2,-1.0]])],"derivedFrom":subQ1}),1.0]])]});}
            var Q55;
            {var subQ0=sQuery(id+"F0.wireOp",EDGE,"E33");var subQ1=sQuery(id+"F0.wireOp",EDGE,"E12");var subQ2=makeQuery(id+"F0.imprint","INTERSECT",VERTEX,{"derivedFrom":[subQ1,subQ0]});Q55=makeQuery(id+"F0.imprint","IMPRINT",FACE,{"disambiguationData":[TD([[makeQuery(id+"F0.imprint","IMPRINT",EDGE,{"disambiguationData":[TD([[subQ2,-1.0]])],"derivedFrom":subQ1}),1.0]])]});}
            var Q56;
            {var subQ0=sQuery(id+"F0.wireOp",EDGE,"E24");var subQ1=sQuery(id+"F0.wireOp",EDGE,"E8");var subQ2=makeQuery(id+"F0.imprint","INTERSECT",VERTEX,{"derivedFrom":[subQ1,subQ0]});Q56=makeQuery(id+"F0.imprint","IMPRINT",FACE,{"disambiguationData":[TD([[makeQuery(id+"F0.imprint","IMPRINT",EDGE,{"disambiguationData":[TD([[subQ2,-1.0]])],"derivedFrom":subQ1}),1.0]])]});}
            var Q57;
            {var subQ0=sQuery(id+"F0.wireOp",EDGE,"E22");var subQ1=sQuery(id+"F0.wireOp",EDGE,"E13");var subQ2=makeQuery(id+"F0.imprint","INTERSECT",VERTEX,{"derivedFrom":[subQ1,subQ0]});Q57=makeQuery(id+"F0.imprint","IMPRINT",FACE,{"disambiguationData":[TD([[makeQuery(id+"F0.imprint","IMPRINT",EDGE,{"disambiguationData":[TD([[subQ2,-1.0]])],"derivedFrom":subQ1}),1.0]])]});}
            var Q58;
            {var subQ0=sQuery(id+"F0.wireOp",EDGE,"E19");var subQ1=sQuery(id+"F0.wireOp",EDGE,"E14");var subQ2=makeQuery(id+"F0.imprint","INTERSECT",VERTEX,{"derivedFrom":[subQ1,subQ0]});Q58=makeQuery(id+"F0.imprint","IMPRINT",FACE,{"disambiguationData":[TD([[makeQuery(id+"F0.imprint","IMPRINT",EDGE,{"disambiguationData":[TD([[subQ2,-1.0]])],"derivedFrom":subQ1}),1.0]])]});}
            var Q59;
            {var subQ0=sQuery(id+"F0.wireOp",EDGE,"E26");var subQ1=sQuery(id+"F0.wireOp",EDGE,"E3");var subQ2=makeQuery(id+"F0.imprint","INTERSECT",VERTEX,{"derivedFrom":[subQ1,subQ0]});Q59=makeQuery(id+"F0.imprint","IMPRINT",FACE,{"disambiguationData":[TD([[makeQuery(id+"F0.imprint","IMPRINT",EDGE,{"disambiguationData":[TD([[subQ2,-1.0]])],"derivedFrom":subQ1}),1.0]])]});}
            var Q60;
            {var subQ0=sQuery(id+"F0.wireOp",EDGE,"E32");var subQ1=sQuery(id+"F0.wireOp",EDGE,"E16");var subQ2=makeQuery(id+"F0.imprint","INTERSECT",VERTEX,{"derivedFrom":[subQ1,subQ0]});Q60=makeQuery(id+"F0.imprint","IMPRINT",FACE,{"disambiguationData":[TD([[makeQuery(id+"F0.imprint","IMPRINT",EDGE,{"disambiguationData":[TD([[subQ2,-1.0]])],"derivedFrom":subQ1}),1.0]])]});}
            var Q61;
            {var subQ0=sQuery(id+"F0.wireOp",EDGE,"E32");var subQ1=sQuery(id+"F0.wireOp",EDGE,"E3");var subQ2=makeQuery(id+"F0.imprint","INTERSECT",VERTEX,{"derivedFrom":[subQ1,subQ0]});Q61=makeQuery(id+"F0.imprint","IMPRINT",FACE,{"disambiguationData":[TD([[makeQuery(id+"F0.imprint","IMPRINT",EDGE,{"disambiguationData":[TD([[subQ2,-1.0]])],"derivedFrom":subQ1}),1.0]])]});}
            var Q62;
            {var subQ0=sQuery(id+"F0.wireOp",EDGE,"E32");var subQ1=sQuery(id+"F0.wireOp",EDGE,"E6");var subQ2=makeQuery(id+"F0.imprint","INTERSECT",VERTEX,{"derivedFrom":[subQ1,subQ0]});Q62=makeQuery(id+"F0.imprint","IMPRINT",FACE,{"disambiguationData":[TD([[makeQuery(id+"F0.imprint","IMPRINT",EDGE,{"disambiguationData":[TD([[subQ2,-1.0]])],"derivedFrom":subQ1}),1.0]])]});}
            var Q63;
            {var subQ0=sQuery(id+"F0.wireOp",EDGE,"E35");var subQ1=sQuery(id+"F0.wireOp",EDGE,"E10");var subQ2=makeQuery(id+"F0.imprint","INTERSECT",VERTEX,{"derivedFrom":[subQ1,subQ0]});Q63=makeQuery(id+"F0.imprint","IMPRINT",FACE,{"disambiguationData":[TD([[makeQuery(id+"F0.imprint","IMPRINT",EDGE,{"disambiguationData":[TD([[subQ2,-1.0]])],"derivedFrom":subQ1}),1.0]])]});}
            var Q64;
            {var subQ0=sQuery(id+"F0.wireOp",EDGE,"E23");var subQ1=sQuery(id+"F0.wireOp",EDGE,"E12");var subQ2=makeQuery(id+"F0.imprint","INTERSECT",VERTEX,{"derivedFrom":[subQ1,subQ0]});Q64=makeQuery(id+"F0.imprint","IMPRINT",FACE,{"disambiguationData":[TD([[makeQuery(id+"F0.imprint","IMPRINT",EDGE,{"disambiguationData":[TD([[subQ2,-1.0]])],"derivedFrom":subQ1}),1.0]])]});}
            var Q65;
            {var subQ0=sQuery(id+"F0.wireOp",EDGE,"E32");var subQ1=sQuery(id+"F0.wireOp",EDGE,"E5");var subQ2=makeQuery(id+"F0.imprint","INTERSECT",VERTEX,{"derivedFrom":[subQ1,subQ0]});Q65=makeQuery(id+"F0.imprint","IMPRINT",FACE,{"disambiguationData":[TD([[makeQuery(id+"F0.imprint","IMPRINT",EDGE,{"disambiguationData":[TD([[subQ2,-1.0]])],"derivedFrom":subQ1}),1.0]])]});}
            var Q66;
            {var subQ0=sQuery(id+"F0.wireOp",EDGE,"E33");var subQ1=sQuery(id+"F0.wireOp",EDGE,"E6");var subQ2=makeQuery(id+"F0.imprint","INTERSECT",VERTEX,{"derivedFrom":[subQ1,subQ0]});Q66=makeQuery(id+"F0.imprint","IMPRINT",FACE,{"disambiguationData":[TD([[makeQuery(id+"F0.imprint","IMPRINT",EDGE,{"disambiguationData":[TD([[subQ2,-1.0]])],"derivedFrom":subQ1}),1.0]])]});}
            var Q67;
            {var subQ0=sQuery(id+"F0.wireOp",EDGE,"E30");var subQ1=sQuery(id+"F0.wireOp",EDGE,"E7");var subQ2=makeQuery(id+"F0.imprint","INTERSECT",VERTEX,{"derivedFrom":[subQ1,subQ0]});Q67=makeQuery(id+"F0.imprint","IMPRINT",FACE,{"disambiguationData":[TD([[makeQuery(id+"F0.imprint","IMPRINT",EDGE,{"disambiguationData":[TD([[subQ2,-1.0]])],"derivedFrom":subQ1}),1.0]])]});}
            var Q68;
            {var subQ0=sQuery(id+"F0.wireOp",EDGE,"E33");var subQ1=sQuery(id+"F0.wireOp",EDGE,"E10");var subQ2=makeQuery(id+"F0.imprint","INTERSECT",VERTEX,{"derivedFrom":[subQ1,subQ0]});Q68=makeQuery(id+"F0.imprint","IMPRINT",FACE,{"disambiguationData":[TD([[makeQuery(id+"F0.imprint","IMPRINT",EDGE,{"disambiguationData":[TD([[subQ2,-1.0]])],"derivedFrom":subQ1}),1.0]])]});}
            var Q69;
            {var subQ0=sQuery(id+"F0.wireOp",EDGE,"E30");var subQ1=sQuery(id+"F0.wireOp",EDGE,"E14");var subQ2=makeQuery(id+"F0.imprint","INTERSECT",VERTEX,{"derivedFrom":[subQ1,subQ0]});Q69=makeQuery(id+"F0.imprint","IMPRINT",FACE,{"disambiguationData":[TD([[makeQuery(id+"F0.imprint","IMPRINT",EDGE,{"disambiguationData":[TD([[subQ2,-1.0]])],"derivedFrom":subQ1}),1.0]])]});}
            var Q70;
            {var subQ0=sQuery(id+"F0.wireOp",EDGE,"E26");var subQ1=sQuery(id+"F0.wireOp",EDGE,"E13");var subQ2=makeQuery(id+"F0.imprint","INTERSECT",VERTEX,{"derivedFrom":[subQ1,subQ0]});Q70=makeQuery(id+"F0.imprint","IMPRINT",FACE,{"disambiguationData":[TD([[makeQuery(id+"F0.imprint","IMPRINT",EDGE,{"disambiguationData":[TD([[subQ2,-1.0]])],"derivedFrom":subQ1}),1.0]])]});}
            var Q71;
            {var subQ0=sQuery(id+"F0.wireOp",EDGE,"E26");var subQ1=sQuery(id+"F0.wireOp",EDGE,"E16");var subQ2=makeQuery(id+"F0.imprint","INTERSECT",VERTEX,{"derivedFrom":[subQ1,subQ0]});Q71=makeQuery(id+"F0.imprint","IMPRINT",FACE,{"disambiguationData":[TD([[makeQuery(id+"F0.imprint","IMPRINT",EDGE,{"disambiguationData":[TD([[subQ2,-1.0]])],"derivedFrom":subQ1}),1.0]])]});}
            var Q72;
            {var subQ0=sQuery(id+"F0.wireOp",EDGE,"E32");var subQ1=sQuery(id+"F0.wireOp",EDGE,"E14");var subQ2=makeQuery(id+"F0.imprint","INTERSECT",VERTEX,{"derivedFrom":[subQ1,subQ0]});Q72=makeQuery(id+"F0.imprint","IMPRINT",FACE,{"disambiguationData":[TD([[makeQuery(id+"F0.imprint","IMPRINT",EDGE,{"disambiguationData":[TD([[subQ2,-1.0]])],"derivedFrom":subQ1}),1.0]])]});}
            var Q73;
            {var subQ0=sQuery(id+"F0.wireOp",EDGE,"E24");var subQ1=sQuery(id+"F0.wireOp",EDGE,"E11");var subQ2=makeQuery(id+"F0.imprint","INTERSECT",VERTEX,{"derivedFrom":[subQ1,subQ0]});Q73=makeQuery(id+"F0.imprint","IMPRINT",FACE,{"disambiguationData":[TD([[makeQuery(id+"F0.imprint","IMPRINT",EDGE,{"disambiguationData":[TD([[subQ2,-1.0]])],"derivedFrom":subQ1}),1.0]])]});}
            var Q74;
            {var subQ0=sQuery(id+"F0.wireOp",EDGE,"E30");var subQ1=sQuery(id+"F0.wireOp",EDGE,"E3");var subQ2=makeQuery(id+"F0.imprint","INTERSECT",VERTEX,{"derivedFrom":[subQ1,subQ0]});Q74=makeQuery(id+"F0.imprint","IMPRINT",FACE,{"disambiguationData":[TD([[makeQuery(id+"F0.imprint","IMPRINT",EDGE,{"disambiguationData":[TD([[subQ2,-1.0]])],"derivedFrom":subQ1}),1.0]])]});}
            var Q75;
            {var subQ0=sQuery(id+"F0.wireOp",EDGE,"E22");var subQ1=sQuery(id+"F0.wireOp",EDGE,"E14");var subQ2=makeQuery(id+"F0.imprint","INTERSECT",VERTEX,{"derivedFrom":[subQ1,subQ0]});Q75=makeQuery(id+"F0.imprint","IMPRINT",FACE,{"disambiguationData":[TD([[makeQuery(id+"F0.imprint","IMPRINT",EDGE,{"disambiguationData":[TD([[subQ2,-1.0]])],"derivedFrom":subQ1}),1.0]])]});}
            var Q76;
            {var subQ0=sQuery(id+"F0.wireOp",EDGE,"E22");var subQ1=sQuery(id+"F0.wireOp",EDGE,"E15");var subQ2=makeQuery(id+"F0.imprint","INTERSECT",VERTEX,{"derivedFrom":[subQ1,subQ0]});Q76=makeQuery(id+"F0.imprint","IMPRINT",FACE,{"disambiguationData":[TD([[makeQuery(id+"F0.imprint","IMPRINT",EDGE,{"disambiguationData":[TD([[subQ2,-1.0]])],"derivedFrom":subQ1}),1.0]])]});}
            var Q77;
            {var subQ0=sQuery(id+"F0.wireOp",EDGE,"E29");var subQ1=sQuery(id+"F0.wireOp",EDGE,"E16");var subQ2=makeQuery(id+"F0.imprint","INTERSECT",VERTEX,{"derivedFrom":[subQ1,subQ0]});Q77=makeQuery(id+"F0.imprint","IMPRINT",FACE,{"disambiguationData":[TD([[makeQuery(id+"F0.imprint","IMPRINT",EDGE,{"disambiguationData":[TD([[subQ2,-1.0]])],"derivedFrom":subQ1}),1.0]])]});}
            var Q78;
            {var subQ0=sQuery(id+"F0.wireOp",EDGE,"E22");var subQ1=sQuery(id+"F0.wireOp",EDGE,"E17");var subQ2=makeQuery(id+"F0.imprint","INTERSECT",VERTEX,{"derivedFrom":[subQ1,subQ0]});Q78=makeQuery(id+"F0.imprint","IMPRINT",FACE,{"disambiguationData":[TD([[makeQuery(id+"F0.imprint","IMPRINT",EDGE,{"disambiguationData":[TD([[subQ2,-1.0]])],"derivedFrom":subQ1}),1.0]])]});}
            var Q79;
            {var subQ0=sQuery(id+"F0.wireOp",EDGE,"E30");var subQ1=sQuery(id+"F0.wireOp",EDGE,"E6");var subQ2=makeQuery(id+"F0.imprint","INTERSECT",VERTEX,{"derivedFrom":[subQ1,subQ0]});Q79=makeQuery(id+"F0.imprint","IMPRINT",FACE,{"disambiguationData":[TD([[makeQuery(id+"F0.imprint","IMPRINT",EDGE,{"disambiguationData":[TD([[subQ2,-1.0]])],"derivedFrom":subQ1}),1.0]])]});}
            var Q80;
            {var subQ0=sQuery(id+"F0.wireOp",EDGE,"E21");var subQ1=sQuery(id+"F0.wireOp",EDGE,"E10");var subQ2=makeQuery(id+"F0.imprint","INTERSECT",VERTEX,{"derivedFrom":[subQ1,subQ0]});Q80=makeQuery(id+"F0.imprint","IMPRINT",FACE,{"disambiguationData":[TD([[makeQuery(id+"F0.imprint","IMPRINT",EDGE,{"disambiguationData":[TD([[subQ2,-1.0]])],"derivedFrom":subQ1}),1.0]])]});}
            var Q81;
            {var subQ0=sQuery(id+"F0.wireOp",EDGE,"E23");var subQ1=sQuery(id+"F0.wireOp",EDGE,"E10");var subQ2=makeQuery(id+"F0.imprint","INTERSECT",VERTEX,{"derivedFrom":[subQ1,subQ0]});Q81=makeQuery(id+"F0.imprint","IMPRINT",FACE,{"disambiguationData":[TD([[makeQuery(id+"F0.imprint","IMPRINT",EDGE,{"disambiguationData":[TD([[subQ2,-1.0]])],"derivedFrom":subQ1}),1.0]])]});}
            var Q82;
            {var subQ0=sQuery(id+"F0.wireOp",EDGE,"E24");var subQ1=sQuery(id+"F0.wireOp",EDGE,"E6");var subQ2=makeQuery(id+"F0.imprint","INTERSECT",VERTEX,{"derivedFrom":[subQ1,subQ0]});Q82=makeQuery(id+"F0.imprint","IMPRINT",FACE,{"disambiguationData":[TD([[makeQuery(id+"F0.imprint","IMPRINT",EDGE,{"disambiguationData":[TD([[subQ2,-1.0]])],"derivedFrom":subQ1}),1.0]])]});}
            var Q83;
            {var subQ0=sQuery(id+"F0.wireOp",EDGE,"E32");var subQ1=sQuery(id+"F0.wireOp",EDGE,"E1");var subQ2=makeQuery(id+"F0.imprint","INTERSECT",VERTEX,{"derivedFrom":[subQ1,subQ0]});Q83=makeQuery(id+"F0.imprint","IMPRINT",FACE,{"disambiguationData":[TD([[makeQuery(id+"F0.imprint","IMPRINT",EDGE,{"disambiguationData":[TD([[subQ2,-1.0]])],"derivedFrom":subQ1}),1.0]])]});}
            var Q84;
            {var subQ0=sQuery(id+"F0.wireOp",EDGE,"E24");var subQ1=sQuery(id+"F0.wireOp",EDGE,"E12");var subQ2=makeQuery(id+"F0.imprint","INTERSECT",VERTEX,{"derivedFrom":[subQ1,subQ0]});Q84=makeQuery(id+"F0.imprint","IMPRINT",FACE,{"disambiguationData":[TD([[makeQuery(id+"F0.imprint","IMPRINT",EDGE,{"disambiguationData":[TD([[subQ2,-1.0]])],"derivedFrom":subQ1}),1.0]])]});}
            var Q85;
            {var subQ0=sQuery(id+"F0.wireOp",EDGE,"E25");var subQ1=sQuery(id+"F0.wireOp",EDGE,"E2");var subQ2=makeQuery(id+"F0.imprint","INTERSECT",VERTEX,{"derivedFrom":[subQ1,subQ0]});Q85=makeQuery(id+"F0.imprint","IMPRINT",FACE,{"disambiguationData":[TD([[makeQuery(id+"F0.imprint","IMPRINT",EDGE,{"disambiguationData":[TD([[subQ2,-1.0]])],"derivedFrom":subQ1}),1.0]])]});}
            var Q86;
            {var subQ0=sQuery(id+"F0.wireOp",EDGE,"E25");var subQ1=sQuery(id+"F0.wireOp",EDGE,"E14");var subQ2=makeQuery(id+"F0.imprint","INTERSECT",VERTEX,{"derivedFrom":[subQ1,subQ0]});Q86=makeQuery(id+"F0.imprint","IMPRINT",FACE,{"disambiguationData":[TD([[makeQuery(id+"F0.imprint","IMPRINT",EDGE,{"disambiguationData":[TD([[subQ2,-1.0]])],"derivedFrom":subQ1}),1.0]])]});}
            var Q87;
            {var subQ0=sQuery(id+"F0.wireOp",EDGE,"E26");var subQ1=sQuery(id+"F0.wireOp",EDGE,"E6");var subQ2=makeQuery(id+"F0.imprint","INTERSECT",VERTEX,{"derivedFrom":[subQ1,subQ0]});Q87=makeQuery(id+"F0.imprint","IMPRINT",FACE,{"disambiguationData":[TD([[makeQuery(id+"F0.imprint","IMPRINT",EDGE,{"disambiguationData":[TD([[subQ2,-1.0]])],"derivedFrom":subQ1}),1.0]])]});}
            var Q88;
            {var subQ0=sQuery(id+"F0.wireOp",EDGE,"E22");var subQ1=sQuery(id+"F0.wireOp",EDGE,"E3");var subQ2=makeQuery(id+"F0.imprint","INTERSECT",VERTEX,{"derivedFrom":[subQ1,subQ0]});Q88=makeQuery(id+"F0.imprint","IMPRINT",FACE,{"disambiguationData":[TD([[makeQuery(id+"F0.imprint","IMPRINT",EDGE,{"disambiguationData":[TD([[subQ2,-1.0]])],"derivedFrom":subQ1}),1.0]])]});}
            var Q89;
            {var subQ0=sQuery(id+"F0.wireOp",EDGE,"E24");var subQ1=sQuery(id+"F0.wireOp",EDGE,"E13");var subQ2=makeQuery(id+"F0.imprint","INTERSECT",VERTEX,{"derivedFrom":[subQ1,subQ0]});Q89=makeQuery(id+"F0.imprint","IMPRINT",FACE,{"disambiguationData":[TD([[makeQuery(id+"F0.imprint","IMPRINT",EDGE,{"disambiguationData":[TD([[subQ2,-1.0]])],"derivedFrom":subQ1}),1.0]])]});}
            var Q90;
            {var subQ0=sQuery(id+"F0.wireOp",EDGE,"E31");var subQ1=sQuery(id+"F0.wireOp",EDGE,"E10");var subQ2=makeQuery(id+"F0.imprint","INTERSECT",VERTEX,{"derivedFrom":[subQ1,subQ0]});Q90=makeQuery(id+"F0.imprint","IMPRINT",FACE,{"disambiguationData":[TD([[makeQuery(id+"F0.imprint","IMPRINT",EDGE,{"disambiguationData":[TD([[subQ2,-1.0]])],"derivedFrom":subQ1}),1.0]])]});}
            var Q91;
            {var subQ0=sQuery(id+"F0.wireOp",EDGE,"E26");var subQ1=sQuery(id+"F0.wireOp",EDGE,"E8");var subQ2=makeQuery(id+"F0.imprint","INTERSECT",VERTEX,{"derivedFrom":[subQ1,subQ0]});Q91=makeQuery(id+"F0.imprint","IMPRINT",FACE,{"disambiguationData":[TD([[makeQuery(id+"F0.imprint","IMPRINT",EDGE,{"disambiguationData":[TD([[subQ2,-1.0]])],"derivedFrom":subQ1}),1.0]])]});}
            var Q92;
            {var subQ0=sQuery(id+"F0.wireOp",EDGE,"E32");var subQ1=sQuery(id+"F0.wireOp",EDGE,"E12");var subQ2=makeQuery(id+"F0.imprint","INTERSECT",VERTEX,{"derivedFrom":[subQ1,subQ0]});Q92=makeQuery(id+"F0.imprint","IMPRINT",FACE,{"disambiguationData":[TD([[makeQuery(id+"F0.imprint","IMPRINT",EDGE,{"disambiguationData":[TD([[subQ2,-1.0]])],"derivedFrom":subQ1}),1.0]])]});}
            var Q93;
            {var subQ0=sQuery(id+"F0.wireOp",EDGE,"E23");var subQ1=sQuery(id+"F0.wireOp",EDGE,"E6");var subQ2=makeQuery(id+"F0.imprint","INTERSECT",VERTEX,{"derivedFrom":[subQ1,subQ0]});Q93=makeQuery(id+"F0.imprint","IMPRINT",FACE,{"disambiguationData":[TD([[makeQuery(id+"F0.imprint","IMPRINT",EDGE,{"disambiguationData":[TD([[subQ2,-1.0]])],"derivedFrom":subQ1}),1.0]])]});}
            var Q94;
            {var subQ0=sQuery(id+"F0.wireOp",EDGE,"E32");var subQ1=sQuery(id+"F0.wireOp",EDGE,"E8");var subQ2=makeQuery(id+"F0.imprint","INTERSECT",VERTEX,{"derivedFrom":[subQ1,subQ0]});Q94=makeQuery(id+"F0.imprint","IMPRINT",FACE,{"disambiguationData":[TD([[makeQuery(id+"F0.imprint","IMPRINT",EDGE,{"disambiguationData":[TD([[subQ2,-1.0]])],"derivedFrom":subQ1}),1.0]])]});}
            var Q95;
            {var subQ0=sQuery(id+"F0.wireOp",EDGE,"E27");var subQ1=sQuery(id+"F0.wireOp",EDGE,"E14");var subQ2=makeQuery(id+"F0.imprint","INTERSECT",VERTEX,{"derivedFrom":[subQ1,subQ0]});Q95=makeQuery(id+"F0.imprint","IMPRINT",FACE,{"disambiguationData":[TD([[makeQuery(id+"F0.imprint","IMPRINT",EDGE,{"disambiguationData":[TD([[subQ2,-1.0]])],"derivedFrom":subQ1}),1.0]])]});}
            var Q96;
            {var subQ0=sQuery(id+"F0.wireOp",EDGE,"E24");var subQ1=sQuery(id+"F0.wireOp",EDGE,"E3");var subQ2=makeQuery(id+"F0.imprint","INTERSECT",VERTEX,{"derivedFrom":[subQ1,subQ0]});Q96=makeQuery(id+"F0.imprint","IMPRINT",FACE,{"disambiguationData":[TD([[makeQuery(id+"F0.imprint","IMPRINT",EDGE,{"disambiguationData":[TD([[subQ2,-1.0]])],"derivedFrom":subQ1}),1.0]])]});}
            var Q97;
            {var subQ0=sQuery(id+"F0.wireOp",EDGE,"E22");var subQ1=sQuery(id+"F0.wireOp",EDGE,"E1");var subQ2=makeQuery(id+"F0.imprint","INTERSECT",VERTEX,{"derivedFrom":[subQ1,subQ0]});Q97=makeQuery(id+"F0.imprint","IMPRINT",FACE,{"disambiguationData":[TD([[makeQuery(id+"F0.imprint","IMPRINT",EDGE,{"disambiguationData":[TD([[subQ2,-1.0]])],"derivedFrom":subQ1}),1.0]])]});}
            var Q98;
            {var subQ0=sQuery(id+"F0.wireOp",EDGE,"E26");var subQ1=sQuery(id+"F0.wireOp",EDGE,"E17");var subQ2=makeQuery(id+"F0.imprint","INTERSECT",VERTEX,{"derivedFrom":[subQ1,subQ0]});Q98=makeQuery(id+"F0.imprint","IMPRINT",FACE,{"disambiguationData":[TD([[makeQuery(id+"F0.imprint","IMPRINT",EDGE,{"disambiguationData":[TD([[subQ2,-1.0]])],"derivedFrom":subQ1}),1.0]])]});}
            var Q99;
            {var subQ0=sQuery(id+"F0.wireOp",EDGE,"E32");var subQ1=sQuery(id+"F0.wireOp",EDGE,"E15");var subQ2=makeQuery(id+"F0.imprint","INTERSECT",VERTEX,{"derivedFrom":[subQ1,subQ0]});Q99=makeQuery(id+"F0.imprint","IMPRINT",FACE,{"disambiguationData":[TD([[makeQuery(id+"F0.imprint","IMPRINT",EDGE,{"disambiguationData":[TD([[subQ2,-1.0]])],"derivedFrom":subQ1}),1.0]])]});}
            var Q100;
            {var subQ0=sQuery(id+"F0.wireOp",EDGE,"E23");var subQ1=sQuery(id+"F0.wireOp",EDGE,"E8");var subQ2=makeQuery(id+"F0.imprint","INTERSECT",VERTEX,{"derivedFrom":[subQ1,subQ0]});Q100=makeQuery(id+"F0.imprint","IMPRINT",FACE,{"disambiguationData":[TD([[makeQuery(id+"F0.imprint","IMPRINT",EDGE,{"disambiguationData":[TD([[subQ2,-1.0]])],"derivedFrom":subQ1}),1.0]])]});}
            var Q101;
            {var subQ0=sQuery(id+"F0.wireOp",EDGE,"E25");var subQ1=sQuery(id+"F0.wireOp",EDGE,"E12");var subQ2=makeQuery(id+"F0.imprint","INTERSECT",VERTEX,{"derivedFrom":[subQ1,subQ0]});Q101=makeQuery(id+"F0.imprint","IMPRINT",FACE,{"disambiguationData":[TD([[makeQuery(id+"F0.imprint","IMPRINT",EDGE,{"disambiguationData":[TD([[subQ2,-1.0]])],"derivedFrom":subQ1}),1.0]])]});}
            var Q102;
            {var subQ0=sQuery(id+"F0.wireOp",EDGE,"E26");var subQ1=sQuery(id+"F0.wireOp",EDGE,"E7");var subQ2=makeQuery(id+"F0.imprint","INTERSECT",VERTEX,{"derivedFrom":[subQ1,subQ0]});Q102=makeQuery(id+"F0.imprint","IMPRINT",FACE,{"disambiguationData":[TD([[makeQuery(id+"F0.imprint","IMPRINT",EDGE,{"disambiguationData":[TD([[subQ2,-1.0]])],"derivedFrom":subQ1}),1.0]])]});}
            var Q103;
            {var subQ0=sQuery(id+"F0.wireOp",EDGE,"E22");var subQ1=sQuery(id+"F0.wireOp",EDGE,"E6");var subQ2=makeQuery(id+"F0.imprint","INTERSECT",VERTEX,{"derivedFrom":[subQ1,subQ0]});Q103=makeQuery(id+"F0.imprint","IMPRINT",FACE,{"disambiguationData":[TD([[makeQuery(id+"F0.imprint","IMPRINT",EDGE,{"disambiguationData":[TD([[subQ2,-1.0]])],"derivedFrom":subQ1}),1.0]])]});}
            var Q104;
            {var subQ0=sQuery(id+"F0.wireOp",EDGE,"E33");var subQ1=sQuery(id+"F0.wireOp",EDGE,"E2");var subQ2=makeQuery(id+"F0.imprint","INTERSECT",VERTEX,{"derivedFrom":[subQ1,subQ0]});Q104=makeQuery(id+"F0.imprint","IMPRINT",FACE,{"disambiguationData":[TD([[makeQuery(id+"F0.imprint","IMPRINT",EDGE,{"disambiguationData":[TD([[subQ2,-1.0]])],"derivedFrom":subQ1}),1.0]])]});}
            var Q105;
            {var subQ0=sQuery(id+"F0.wireOp",EDGE,"E21");var subQ1=sQuery(id+"F0.wireOp",EDGE,"E8");var subQ2=makeQuery(id+"F0.imprint","INTERSECT",VERTEX,{"derivedFrom":[subQ1,subQ0]});Q105=makeQuery(id+"F0.imprint","IMPRINT",FACE,{"disambiguationData":[TD([[makeQuery(id+"F0.imprint","IMPRINT",EDGE,{"disambiguationData":[TD([[subQ2,-1.0]])],"derivedFrom":subQ1}),1.0]])]});}
            var Q106;
            {var subQ0=sQuery(id+"F0.wireOp",EDGE,"E22");var subQ1=sQuery(id+"F0.wireOp",EDGE,"E11");var subQ2=makeQuery(id+"F0.imprint","INTERSECT",VERTEX,{"derivedFrom":[subQ1,subQ0]});Q106=makeQuery(id+"F0.imprint","IMPRINT",FACE,{"disambiguationData":[TD([[makeQuery(id+"F0.imprint","IMPRINT",EDGE,{"disambiguationData":[TD([[subQ2,-1.0]])],"derivedFrom":subQ1}),1.0]])]});}
            var Q107;
            {var subQ0=sQuery(id+"F0.wireOp",EDGE,"E32");var subQ1=sQuery(id+"F0.wireOp",EDGE,"E13");var subQ2=makeQuery(id+"F0.imprint","INTERSECT",VERTEX,{"derivedFrom":[subQ1,subQ0]});Q107=makeQuery(id+"F0.imprint","IMPRINT",FACE,{"disambiguationData":[TD([[makeQuery(id+"F0.imprint","IMPRINT",EDGE,{"disambiguationData":[TD([[subQ2,-1.0]])],"derivedFrom":subQ1}),1.0]])]});}
            var Q108;
            {var subQ0=sQuery(id+"F0.wireOp",EDGE,"E21");var subQ1=sQuery(id+"F0.wireOp",EDGE,"E14");var subQ2=makeQuery(id+"F0.imprint","INTERSECT",VERTEX,{"derivedFrom":[subQ1,subQ0]});Q108=makeQuery(id+"F0.imprint","IMPRINT",FACE,{"disambiguationData":[TD([[makeQuery(id+"F0.imprint","IMPRINT",EDGE,{"disambiguationData":[TD([[subQ2,-1.0]])],"derivedFrom":subQ1}),1.0]])]});}
            var Q109;
            {var subQ0=sQuery(id+"F0.wireOp",EDGE,"E29");var subQ1=sQuery(id+"F0.wireOp",EDGE,"E6");var subQ2=makeQuery(id+"F0.imprint","INTERSECT",VERTEX,{"derivedFrom":[subQ1,subQ0]});Q109=makeQuery(id+"F0.imprint","IMPRINT",FACE,{"disambiguationData":[TD([[makeQuery(id+"F0.imprint","IMPRINT",EDGE,{"disambiguationData":[TD([[subQ2,-1.0]])],"derivedFrom":subQ1}),1.0]])]});}
            var Q110;
            {var subQ0=sQuery(id+"F0.wireOp",EDGE,"E30");var subQ1=sQuery(id+"F0.wireOp",EDGE,"E1");var subQ2=makeQuery(id+"F0.imprint","INTERSECT",VERTEX,{"derivedFrom":[subQ1,subQ0]});Q110=makeQuery(id+"F0.imprint","IMPRINT",FACE,{"disambiguationData":[TD([[makeQuery(id+"F0.imprint","IMPRINT",EDGE,{"disambiguationData":[TD([[subQ2,-1.0]])],"derivedFrom":subQ1}),1.0]])]});}
            var Q111;
            {var subQ0=sQuery(id+"F0.wireOp",EDGE,"E35");var subQ1=sQuery(id+"F0.wireOp",EDGE,"E6");var subQ2=makeQuery(id+"F0.imprint","INTERSECT",VERTEX,{"derivedFrom":[subQ1,subQ0]});Q111=makeQuery(id+"F0.imprint","IMPRINT",FACE,{"disambiguationData":[TD([[makeQuery(id+"F0.imprint","IMPRINT",EDGE,{"disambiguationData":[TD([[subQ2,-1.0]])],"derivedFrom":subQ1}),1.0]])]});}
            var Q112;
            {var subQ0=sQuery(id+"F0.wireOp",EDGE,"E19");var subQ1=sQuery(id+"F0.wireOp",EDGE,"E6");var subQ2=makeQuery(id+"F0.imprint","INTERSECT",VERTEX,{"derivedFrom":[subQ1,subQ0]});Q112=makeQuery(id+"F0.imprint","IMPRINT",FACE,{"disambiguationData":[TD([[makeQuery(id+"F0.imprint","IMPRINT",EDGE,{"disambiguationData":[TD([[subQ2,-1.0]])],"derivedFrom":subQ1}),1.0]])]});}
            var Q113;
            {var subQ0=sQuery(id+"F0.wireOp",EDGE,"E30");var subQ1=sQuery(id+"F0.wireOp",EDGE,"E8");var subQ2=makeQuery(id+"F0.imprint","INTERSECT",VERTEX,{"derivedFrom":[subQ1,subQ0]});Q113=makeQuery(id+"F0.imprint","IMPRINT",FACE,{"disambiguationData":[TD([[makeQuery(id+"F0.imprint","IMPRINT",EDGE,{"disambiguationData":[TD([[subQ2,-1.0]])],"derivedFrom":subQ1}),1.0]])]});}
            var Q114;
            {var subQ0=sQuery(id+"F0.wireOp",EDGE,"E30");var subQ1=sQuery(id+"F0.wireOp",EDGE,"E2");var subQ2=makeQuery(id+"F0.imprint","INTERSECT",VERTEX,{"derivedFrom":[subQ1,subQ0]});Q114=makeQuery(id+"F0.imprint","IMPRINT",FACE,{"disambiguationData":[TD([[makeQuery(id+"F0.imprint","IMPRINT",EDGE,{"disambiguationData":[TD([[subQ2,-1.0]])],"derivedFrom":subQ1}),1.0]])]});}
            var Q115;
            {var subQ0=sQuery(id+"F0.wireOp",EDGE,"E26");var subQ1=sQuery(id+"F0.wireOp",EDGE,"E2");var subQ2=makeQuery(id+"F0.imprint","INTERSECT",VERTEX,{"derivedFrom":[subQ1,subQ0]});Q115=makeQuery(id+"F0.imprint","IMPRINT",FACE,{"disambiguationData":[TD([[makeQuery(id+"F0.imprint","IMPRINT",EDGE,{"disambiguationData":[TD([[subQ2,-1.0]])],"derivedFrom":subQ1}),1.0]])]});}
            var Q116;
            {var subQ0=sQuery(id+"F0.wireOp",EDGE,"E21");var subQ1=sQuery(id+"F0.wireOp",EDGE,"E2");var subQ2=makeQuery(id+"F0.imprint","INTERSECT",VERTEX,{"derivedFrom":[subQ1,subQ0]});Q116=makeQuery(id+"F0.imprint","IMPRINT",FACE,{"disambiguationData":[TD([[makeQuery(id+"F0.imprint","IMPRINT",EDGE,{"disambiguationData":[TD([[subQ2,-1.0]])],"derivedFrom":subQ1}),1.0]])]});}
            var Q117;
            {var subQ0=sQuery(id+"F0.wireOp",EDGE,"E27");var subQ1=sQuery(id+"F0.wireOp",EDGE,"E6");var subQ2=makeQuery(id+"F0.imprint","INTERSECT",VERTEX,{"derivedFrom":[subQ1,subQ0]});Q117=makeQuery(id+"F0.imprint","IMPRINT",FACE,{"disambiguationData":[TD([[makeQuery(id+"F0.imprint","IMPRINT",EDGE,{"disambiguationData":[TD([[subQ2,-1.0]])],"derivedFrom":subQ1}),1.0]])]});}
            var Q118;
            {var subQ0=sQuery(id+"F0.wireOp",EDGE,"E19");var subQ1=sQuery(id+"F0.wireOp",EDGE,"E8");var subQ2=makeQuery(id+"F0.imprint","INTERSECT",VERTEX,{"derivedFrom":[subQ1,subQ0]});Q118=makeQuery(id+"F0.imprint","IMPRINT",FACE,{"disambiguationData":[TD([[makeQuery(id+"F0.imprint","IMPRINT",EDGE,{"disambiguationData":[TD([[subQ2,-1.0]])],"derivedFrom":subQ1}),1.0]])]});}
            var Q119;
            {var subQ0=sQuery(id+"F0.wireOp",EDGE,"E30");var subQ1=sQuery(id+"F0.wireOp",EDGE,"E16");var subQ2=makeQuery(id+"F0.imprint","INTERSECT",VERTEX,{"derivedFrom":[subQ1,subQ0]});Q119=makeQuery(id+"F0.imprint","IMPRINT",FACE,{"disambiguationData":[TD([[makeQuery(id+"F0.imprint","IMPRINT",EDGE,{"disambiguationData":[TD([[subQ2,-1.0]])],"derivedFrom":subQ1}),1.0]])]});}
            var Q120;
            {var subQ0=sQuery(id+"F0.wireOp",EDGE,"E24");var subQ1=sQuery(id+"F0.wireOp",EDGE,"E16");var subQ2=makeQuery(id+"F0.imprint","INTERSECT",VERTEX,{"derivedFrom":[subQ1,subQ0]});Q120=makeQuery(id+"F0.imprint","IMPRINT",FACE,{"disambiguationData":[TD([[makeQuery(id+"F0.imprint","IMPRINT",EDGE,{"disambiguationData":[TD([[subQ2,-1.0]])],"derivedFrom":subQ1}),1.0]])]});}
            var Q121;
            {var subQ0=sQuery(id+"F0.wireOp",EDGE,"E19");var subQ1=sQuery(id+"F0.wireOp",EDGE,"E12");var subQ2=makeQuery(id+"F0.imprint","INTERSECT",VERTEX,{"derivedFrom":[subQ1,subQ0]});Q121=makeQuery(id+"F0.imprint","IMPRINT",FACE,{"disambiguationData":[TD([[makeQuery(id+"F0.imprint","IMPRINT",EDGE,{"disambiguationData":[TD([[subQ2,-1.0]])],"derivedFrom":subQ1}),1.0]])]});}
            var Q122;
            {var subQ0=sQuery(id+"F0.wireOp",EDGE,"E22");var subQ1=sQuery(id+"F0.wireOp",EDGE,"E2");var subQ2=makeQuery(id+"F0.imprint","INTERSECT",VERTEX,{"derivedFrom":[subQ1,subQ0]});Q122=makeQuery(id+"F0.imprint","IMPRINT",FACE,{"disambiguationData":[TD([[makeQuery(id+"F0.imprint","IMPRINT",EDGE,{"disambiguationData":[TD([[subQ2,-1.0]])],"derivedFrom":subQ1}),1.0]])]});}
            var Q123;
            {var subQ0=sQuery(id+"F0.wireOp",EDGE,"E27");var subQ1=sQuery(id+"F0.wireOp",EDGE,"E8");var subQ2=makeQuery(id+"F0.imprint","INTERSECT",VERTEX,{"derivedFrom":[subQ1,subQ0]});Q123=makeQuery(id+"F0.imprint","IMPRINT",FACE,{"disambiguationData":[TD([[makeQuery(id+"F0.imprint","IMPRINT",EDGE,{"disambiguationData":[TD([[subQ2,-1.0]])],"derivedFrom":subQ1}),1.0]])]});}
            var Q124;
            {var subQ0=sQuery(id+"F0.wireOp",EDGE,"E22");var subQ1=sQuery(id+"F0.wireOp",EDGE,"E7");var subQ2=makeQuery(id+"F0.imprint","INTERSECT",VERTEX,{"derivedFrom":[subQ1,subQ0]});Q124=makeQuery(id+"F0.imprint","IMPRINT",FACE,{"disambiguationData":[TD([[makeQuery(id+"F0.imprint","IMPRINT",EDGE,{"disambiguationData":[TD([[subQ2,-1.0]])],"derivedFrom":subQ1}),1.0]])]});}
            var Q125;
            {var subQ0=sQuery(id+"F0.wireOp",EDGE,"E26");var subQ1=sQuery(id+"F0.wireOp",EDGE,"E10");var subQ2=makeQuery(id+"F0.imprint","INTERSECT",VERTEX,{"derivedFrom":[subQ1,subQ0]});Q125=makeQuery(id+"F0.imprint","IMPRINT",FACE,{"disambiguationData":[TD([[makeQuery(id+"F0.imprint","IMPRINT",EDGE,{"disambiguationData":[TD([[subQ2,-1.0]])],"derivedFrom":subQ1}),1.0]])]});}
            var Q126;
            {var subQ0=sQuery(id+"F0.wireOp",EDGE,"E25");var subQ1=sQuery(id+"F0.wireOp",EDGE,"E10");var subQ2=makeQuery(id+"F0.imprint","INTERSECT",VERTEX,{"derivedFrom":[subQ1,subQ0]});Q126=makeQuery(id+"F0.imprint","IMPRINT",FACE,{"disambiguationData":[TD([[makeQuery(id+"F0.imprint","IMPRINT",EDGE,{"disambiguationData":[TD([[subQ2,-1.0]])],"derivedFrom":subQ1}),1.0]])]});}
            var Q127;
            {var subQ0=sQuery(id+"F0.wireOp",EDGE,"E21");var subQ1=sQuery(id+"F0.wireOp",EDGE,"E6");var subQ2=makeQuery(id+"F0.imprint","INTERSECT",VERTEX,{"derivedFrom":[subQ1,subQ0]});Q127=makeQuery(id+"F0.imprint","IMPRINT",FACE,{"disambiguationData":[TD([[makeQuery(id+"F0.imprint","IMPRINT",EDGE,{"disambiguationData":[TD([[subQ2,-1.0]])],"derivedFrom":subQ1}),1.0]])]});}
            var Q128;
            {var subQ0=sQuery(id+"F0.wireOp",EDGE,"E29");var subQ1=sQuery(id+"F0.wireOp",EDGE,"E2");var subQ2=makeQuery(id+"F0.imprint","INTERSECT",VERTEX,{"derivedFrom":[subQ1,subQ0]});Q128=makeQuery(id+"F0.imprint","IMPRINT",FACE,{"disambiguationData":[TD([[makeQuery(id+"F0.imprint","IMPRINT",EDGE,{"disambiguationData":[TD([[subQ2,-1.0]])],"derivedFrom":subQ1}),1.0]])]});}
            var Q129;
            {var subQ0=sQuery(id+"F0.wireOp",EDGE,"E27");var subQ1=sQuery(id+"F0.wireOp",EDGE,"E12");var subQ2=makeQuery(id+"F0.imprint","INTERSECT",VERTEX,{"derivedFrom":[subQ1,subQ0]});Q129=makeQuery(id+"F0.imprint","IMPRINT",FACE,{"disambiguationData":[TD([[makeQuery(id+"F0.imprint","IMPRINT",EDGE,{"disambiguationData":[TD([[subQ2,-1.0]])],"derivedFrom":subQ1}),1.0]])]});}
            var Q130;
            {var subQ0=sQuery(id+"F0.wireOp",EDGE,"E32");var subQ1=sQuery(id+"F0.wireOp",EDGE,"E2");var subQ2=makeQuery(id+"F0.imprint","INTERSECT",VERTEX,{"derivedFrom":[subQ1,subQ0]});Q130=makeQuery(id+"F0.imprint","IMPRINT",FACE,{"disambiguationData":[TD([[makeQuery(id+"F0.imprint","IMPRINT",EDGE,{"disambiguationData":[TD([[subQ2,-1.0]])],"derivedFrom":subQ1}),1.0]])]});}
            var Q131;
            {var subQ0=sQuery(id+"F0.wireOp",EDGE,"E22");var subQ1=sQuery(id+"F0.wireOp",EDGE,"E12");var subQ2=makeQuery(id+"F0.imprint","INTERSECT",VERTEX,{"derivedFrom":[subQ1,subQ0]});Q131=makeQuery(id+"F0.imprint","IMPRINT",FACE,{"disambiguationData":[TD([[makeQuery(id+"F0.imprint","IMPRINT",EDGE,{"disambiguationData":[TD([[subQ2,-1.0]])],"derivedFrom":subQ1}),1.0]])]});}
            var Q132;
            {var subQ0=sQuery(id+"F0.wireOp",EDGE,"E23");var subQ1=sQuery(id+"F0.wireOp",EDGE,"E2");var subQ2=makeQuery(id+"F0.imprint","INTERSECT",VERTEX,{"derivedFrom":[subQ1,subQ0]});Q132=makeQuery(id+"F0.imprint","IMPRINT",FACE,{"disambiguationData":[TD([[makeQuery(id+"F0.imprint","IMPRINT",EDGE,{"disambiguationData":[TD([[subQ2,-1.0]])],"derivedFrom":subQ1}),1.0]])]});}
            var Q133;
            {var subQ0=sQuery(id+"F0.wireOp",EDGE,"E22");var subQ1=sQuery(id+"F0.wireOp",EDGE,"E10");var subQ2=makeQuery(id+"F0.imprint","INTERSECT",VERTEX,{"derivedFrom":[subQ1,subQ0]});Q133=makeQuery(id+"F0.imprint","IMPRINT",FACE,{"disambiguationData":[TD([[makeQuery(id+"F0.imprint","IMPRINT",EDGE,{"disambiguationData":[TD([[subQ2,-1.0]])],"derivedFrom":subQ1}),1.0]])]});}
            var Q134;
            {var subQ0=sQuery(id+"F0.wireOp",EDGE,"E26");var subQ1=sQuery(id+"F0.wireOp",EDGE,"E15");var subQ2=makeQuery(id+"F0.imprint","INTERSECT",VERTEX,{"derivedFrom":[subQ1,subQ0]});Q134=makeQuery(id+"F0.imprint","IMPRINT",FACE,{"disambiguationData":[TD([[makeQuery(id+"F0.imprint","IMPRINT",EDGE,{"disambiguationData":[TD([[subQ2,-1.0]])],"derivedFrom":subQ1}),1.0]])]});}
            var Q135;
            {var subQ0=sQuery(id+"F0.wireOp",EDGE,"E24");var subQ1=sQuery(id+"F0.wireOp",EDGE,"E14");var subQ2=makeQuery(id+"F0.imprint","INTERSECT",VERTEX,{"derivedFrom":[subQ1,subQ0]});Q135=makeQuery(id+"F0.imprint","IMPRINT",FACE,{"disambiguationData":[TD([[makeQuery(id+"F0.imprint","IMPRINT",EDGE,{"disambiguationData":[TD([[subQ2,-1.0]])],"derivedFrom":subQ1}),1.0]])]});}
            var Q136;
            {var subQ0=sQuery(id+"F0.wireOp",EDGE,"E24");var subQ1=sQuery(id+"F0.wireOp",EDGE,"E9");var subQ2=makeQuery(id+"F0.imprint","INTERSECT",VERTEX,{"derivedFrom":[subQ1,subQ0]});Q136=makeQuery(id+"F0.imprint","IMPRINT",FACE,{"disambiguationData":[TD([[makeQuery(id+"F0.imprint","IMPRINT",EDGE,{"disambiguationData":[TD([[subQ2,-1.0]])],"derivedFrom":subQ1}),1.0]])]});}
            var Q137;
            {var subQ0=sQuery(id+"F0.wireOp",EDGE,"E21");var subQ1=sQuery(id+"F0.wireOp",EDGE,"E12");var subQ2=makeQuery(id+"F0.imprint","INTERSECT",VERTEX,{"derivedFrom":[subQ1,subQ0]});Q137=makeQuery(id+"F0.imprint","IMPRINT",FACE,{"disambiguationData":[TD([[makeQuery(id+"F0.imprint","IMPRINT",EDGE,{"disambiguationData":[TD([[subQ2,-1.0]])],"derivedFrom":subQ1}),1.0]])]});}
            var Q138;
            {var subQ0=sQuery(id+"F0.wireOp",EDGE,"E22");var subQ1=sQuery(id+"F0.wireOp",EDGE,"E5");var subQ2=makeQuery(id+"F0.imprint","INTERSECT",VERTEX,{"derivedFrom":[subQ1,subQ0]});Q138=makeQuery(id+"F0.imprint","IMPRINT",FACE,{"disambiguationData":[TD([[makeQuery(id+"F0.imprint","IMPRINT",EDGE,{"disambiguationData":[TD([[subQ2,-1.0]])],"derivedFrom":subQ1}),1.0]])]});}
            var Q139;
            {var subQ0=sQuery(id+"F0.wireOp",EDGE,"E24");var subQ1=sQuery(id+"F0.wireOp",EDGE,"E15");var subQ2=makeQuery(id+"F0.imprint","INTERSECT",VERTEX,{"derivedFrom":[subQ1,subQ0]});Q139=makeQuery(id+"F0.imprint","IMPRINT",FACE,{"disambiguationData":[TD([[makeQuery(id+"F0.imprint","IMPRINT",EDGE,{"disambiguationData":[TD([[subQ2,-1.0]])],"derivedFrom":subQ1}),1.0]])]});}
            var Q140;
            {var subQ0=sQuery(id+"F0.wireOp",EDGE,"E24");var subQ1=sQuery(id+"F0.wireOp",EDGE,"E2");var subQ2=makeQuery(id+"F0.imprint","INTERSECT",VERTEX,{"derivedFrom":[subQ1,subQ0]});Q140=makeQuery(id+"F0.imprint","IMPRINT",FACE,{"disambiguationData":[TD([[makeQuery(id+"F0.imprint","IMPRINT",EDGE,{"disambiguationData":[TD([[subQ2,-1.0]])],"derivedFrom":subQ1}),1.0]])]});}
            var Q141;
            {var subQ0=sQuery(id+"F0.wireOp",EDGE,"E29");var subQ1=sQuery(id+"F0.wireOp",EDGE,"E14");var subQ2=makeQuery(id+"F0.imprint","INTERSECT",VERTEX,{"derivedFrom":[subQ1,subQ0]});Q141=makeQuery(id+"F0.imprint","IMPRINT",FACE,{"disambiguationData":[TD([[makeQuery(id+"F0.imprint","IMPRINT",EDGE,{"disambiguationData":[TD([[subQ2,-1.0]])],"derivedFrom":subQ1}),1.0]])]});}
            var Q142;
            {var subQ0=sQuery(id+"F0.wireOp",EDGE,"E31");var subQ1=sQuery(id+"F0.wireOp",EDGE,"E16");var subQ2=makeQuery(id+"F0.imprint","INTERSECT",VERTEX,{"derivedFrom":[subQ1,subQ0]});Q142=makeQuery(id+"F0.imprint","IMPRINT",FACE,{"disambiguationData":[TD([[makeQuery(id+"F0.imprint","IMPRINT",EDGE,{"disambiguationData":[TD([[subQ2,-1.0]])],"derivedFrom":subQ1}),1.0]])]});}
            var Q143;
            {var subQ0=sQuery(id+"F0.wireOp",EDGE,"E34");var subQ1=sQuery(id+"F0.wireOp",EDGE,"E15");var subQ2=makeQuery(id+"F0.imprint","INTERSECT",VERTEX,{"derivedFrom":[subQ1,subQ0]});Q143=makeQuery(id+"F0.imprint","IMPRINT",FACE,{"disambiguationData":[TD([[makeQuery(id+"F0.imprint","IMPRINT",EDGE,{"disambiguationData":[TD([[subQ2,-1.0]])],"derivedFrom":subQ1}),1.0]])]});}
            var Q144;
            {var subQ0=sQuery(id+"F0.wireOp",EDGE,"E25");var subQ1=sQuery(id+"F0.wireOp",EDGE,"E4");var subQ2=makeQuery(id+"F0.imprint","INTERSECT",VERTEX,{"derivedFrom":[subQ1,subQ0]});Q144=makeQuery(id+"F0.imprint","IMPRINT",FACE,{"disambiguationData":[TD([[makeQuery(id+"F0.imprint","IMPRINT",EDGE,{"disambiguationData":[TD([[subQ2,-1.0]])],"derivedFrom":subQ1}),1.0]])]});}
            var Q145;
            {var subQ0=sQuery(id+"F0.wireOp",EDGE,"E20");var subQ1=sQuery(id+"F0.wireOp",EDGE,"E6");var subQ2=makeQuery(id+"F0.imprint","INTERSECT",VERTEX,{"derivedFrom":[subQ1,subQ0]});Q145=makeQuery(id+"F0.imprint","IMPRINT",FACE,{"disambiguationData":[TD([[makeQuery(id+"F0.imprint","IMPRINT",EDGE,{"disambiguationData":[TD([[subQ2,-1.0]])],"derivedFrom":subQ1}),1.0]])]});}
            var Q146;
            {var subQ0=sQuery(id+"F0.wireOp",EDGE,"E22");var subQ1=sQuery(id+"F0.wireOp",EDGE,"E0.right");var subQ2=makeQuery(id+"F0.imprint","INTERSECT",VERTEX,{"derivedFrom":[subQ1,subQ0]});Q146=makeQuery(id+"F0.imprint","IMPRINT",FACE,{"disambiguationData":[TD([[makeQuery(id+"F0.imprint","IMPRINT",EDGE,{"disambiguationData":[TD([[subQ2,-1.0]])],"derivedFrom":subQ1}),-1.0]])]});}
            var Q147;
            {var subQ0=sQuery(id+"F0.wireOp",EDGE,"E7");var subQ1=sQuery(id+"F0.wireOp",EDGE,"E0.bottom");var subQ2=makeQuery(id+"F0.imprint","INTERSECT",VERTEX,{"derivedFrom":[subQ1,subQ0]});Q147=makeQuery(id+"F0.imprint","IMPRINT",FACE,{"disambiguationData":[TD([[makeQuery(id+"F0.imprint","IMPRINT",EDGE,{"disambiguationData":[TD([[subQ2,-1.0]])],"derivedFrom":subQ1}),-1.0]])]});}
            var Q148;
            {var subQ0=sQuery(id+"F0.wireOp",EDGE,"E20");var subQ1=sQuery(id+"F0.wireOp",EDGE,"E15");var subQ2=makeQuery(id+"F0.imprint","INTERSECT",VERTEX,{"derivedFrom":[subQ1,subQ0]});Q148=makeQuery(id+"F0.imprint","IMPRINT",FACE,{"disambiguationData":[TD([[makeQuery(id+"F0.imprint","IMPRINT",EDGE,{"disambiguationData":[TD([[subQ2,-1.0]])],"derivedFrom":subQ1}),1.0]])]});}
            var Q149;
            {var subQ0=sQuery(id+"F0.wireOp",EDGE,"E30");var subQ1=sQuery(id+"F0.wireOp",EDGE,"E0.left");var subQ2=makeQuery(id+"F0.imprint","INTERSECT",VERTEX,{"derivedFrom":[subQ1,subQ0]});Q149=makeQuery(id+"F0.imprint","IMPRINT",FACE,{"disambiguationData":[TD([[makeQuery(id+"F0.imprint","IMPRINT",EDGE,{"disambiguationData":[TD([[subQ2,-1.0]])],"derivedFrom":subQ1}),1.0]])]});}
            var Q150;
            {var subQ0=sQuery(id+"F0.wireOp",EDGE,"E20");var subQ1=sQuery(id+"F0.wireOp",EDGE,"E1");var subQ2=makeQuery(id+"F0.imprint","INTERSECT",VERTEX,{"derivedFrom":[subQ1,subQ0]});Q150=makeQuery(id+"F0.imprint","IMPRINT",FACE,{"disambiguationData":[TD([[makeQuery(id+"F0.imprint","IMPRINT",EDGE,{"disambiguationData":[TD([[subQ2,-1.0]])],"derivedFrom":subQ1}),1.0]])]});}
            var Q151;
            {var subQ0=sQuery(id+"F0.wireOp",EDGE,"E28");var subQ1=sQuery(id+"F0.wireOp",EDGE,"E12");var subQ2=makeQuery(id+"F0.imprint","INTERSECT",VERTEX,{"derivedFrom":[subQ1,subQ0]});Q151=makeQuery(id+"F0.imprint","IMPRINT",FACE,{"disambiguationData":[TD([[makeQuery(id+"F0.imprint","IMPRINT",EDGE,{"disambiguationData":[TD([[subQ2,-1.0]])],"derivedFrom":subQ1}),1.0]])]});}
            var Q152;
            {var subQ0=sQuery(id+"F0.wireOp",EDGE,"E35");var subQ1=sQuery(id+"F0.wireOp",EDGE,"E0.left");var subQ2=makeQuery(id+"F0.imprint","INTERSECT",VERTEX,{"derivedFrom":[subQ1,subQ0]});Q152=makeQuery(id+"F0.imprint","IMPRINT",FACE,{"disambiguationData":[TD([[makeQuery(id+"F0.imprint","IMPRINT",EDGE,{"disambiguationData":[TD([[subQ2,-1.0]])],"derivedFrom":subQ1}),1.0]])]});}
            var Q153;
            {var subQ0=sQuery(id+"F0.wireOp",EDGE,"E34");var subQ1=sQuery(id+"F0.wireOp",EDGE,"E17");var subQ2=makeQuery(id+"F0.imprint","INTERSECT",VERTEX,{"derivedFrom":[subQ1,subQ0]});Q153=makeQuery(id+"F0.imprint","IMPRINT",FACE,{"disambiguationData":[TD([[makeQuery(id+"F0.imprint","IMPRINT",EDGE,{"disambiguationData":[TD([[subQ2,-1.0]])],"derivedFrom":subQ1}),1.0]])]});}
            var Q154;
            {var subQ0=sQuery(id+"F0.wireOp",EDGE,"E28");var subQ1=sQuery(id+"F0.wireOp",EDGE,"E11");var subQ2=makeQuery(id+"F0.imprint","INTERSECT",VERTEX,{"derivedFrom":[subQ1,subQ0]});Q154=makeQuery(id+"F0.imprint","IMPRINT",FACE,{"disambiguationData":[TD([[makeQuery(id+"F0.imprint","IMPRINT",EDGE,{"disambiguationData":[TD([[subQ2,-1.0]])],"derivedFrom":subQ1}),1.0]])]});}
            var Q155;
            {var subQ0=sQuery(id+"F0.wireOp",EDGE,"E35");var subQ1=sQuery(id+"F0.wireOp",EDGE,"E0.right");var subQ2=makeQuery(id+"F0.imprint","INTERSECT",VERTEX,{"derivedFrom":[subQ1,subQ0]});Q155=makeQuery(id+"F0.imprint","IMPRINT",FACE,{"disambiguationData":[TD([[makeQuery(id+"F0.imprint","IMPRINT",EDGE,{"disambiguationData":[TD([[subQ2,-1.0]])],"derivedFrom":subQ1}),-1.0]])]});}
            var Q156;
            {var subQ0=sQuery(id+"F0.wireOp",EDGE,"E28");var subQ1=sQuery(id+"F0.wireOp",EDGE,"E10");var subQ2=makeQuery(id+"F0.imprint","INTERSECT",VERTEX,{"derivedFrom":[subQ1,subQ0]});Q156=makeQuery(id+"F0.imprint","IMPRINT",FACE,{"disambiguationData":[TD([[makeQuery(id+"F0.imprint","IMPRINT",EDGE,{"disambiguationData":[TD([[subQ2,-1.0]])],"derivedFrom":subQ1}),1.0]])]});}
            var Q157;
            {var subQ0=sQuery(id+"F0.wireOp",EDGE,"E24");var subQ1=sQuery(id+"F0.wireOp",EDGE,"E4");var subQ2=makeQuery(id+"F0.imprint","INTERSECT",VERTEX,{"derivedFrom":[subQ1,subQ0]});Q157=makeQuery(id+"F0.imprint","IMPRINT",FACE,{"disambiguationData":[TD([[makeQuery(id+"F0.imprint","IMPRINT",EDGE,{"disambiguationData":[TD([[subQ2,-1.0]])],"derivedFrom":subQ1}),1.0]])]});}
            var Q158;
            {var subQ0=sQuery(id+"F0.wireOp",EDGE,"E17");var subQ1=sQuery(id+"F0.wireOp",EDGE,"E0.bottom");var subQ2=makeQuery(id+"F0.imprint","INTERSECT",VERTEX,{"derivedFrom":[subQ1,subQ0]});Q158=makeQuery(id+"F0.imprint","IMPRINT",FACE,{"disambiguationData":[TD([[makeQuery(id+"F0.imprint","IMPRINT",EDGE,{"disambiguationData":[TD([[subQ2,-1.0]])],"derivedFrom":subQ1}),-1.0]])]});}
            var Q159;
            {var subQ0=sQuery(id+"F0.wireOp",EDGE,"E13");var subQ1=sQuery(id+"F0.wireOp",EDGE,"E0.bottom");var subQ2=makeQuery(id+"F0.imprint","INTERSECT",VERTEX,{"derivedFrom":[subQ1,subQ0]});Q159=makeQuery(id+"F0.imprint","IMPRINT",FACE,{"disambiguationData":[TD([[makeQuery(id+"F0.imprint","IMPRINT",EDGE,{"disambiguationData":[TD([[subQ2,-1.0]])],"derivedFrom":subQ1}),-1.0]])]});}
            var Q160;
            {var subQ0=sQuery(id+"F0.wireOp",EDGE,"E20");var subQ1=sQuery(id+"F0.wireOp",EDGE,"E5");var subQ2=makeQuery(id+"F0.imprint","INTERSECT",VERTEX,{"derivedFrom":[subQ1,subQ0]});Q160=makeQuery(id+"F0.imprint","IMPRINT",FACE,{"disambiguationData":[TD([[makeQuery(id+"F0.imprint","IMPRINT",EDGE,{"disambiguationData":[TD([[subQ2,-1.0]])],"derivedFrom":subQ1}),1.0]])]});}
            var Q161;
            {var subQ0=sQuery(id+"F0.wireOp",EDGE,"E20");var subQ1=sQuery(id+"F0.wireOp",EDGE,"E16");var subQ2=makeQuery(id+"F0.imprint","INTERSECT",VERTEX,{"derivedFrom":[subQ1,subQ0]});Q161=makeQuery(id+"F0.imprint","IMPRINT",FACE,{"disambiguationData":[TD([[makeQuery(id+"F0.imprint","IMPRINT",EDGE,{"disambiguationData":[TD([[subQ2,-1.0]])],"derivedFrom":subQ1}),1.0]])]});}
            var Q162;
            {var subQ0=sQuery(id+"F0.wireOp",EDGE,"E16");var subQ1=sQuery(id+"F0.wireOp",EDGE,"E0.bottom");var subQ2=makeQuery(id+"F0.imprint","INTERSECT",VERTEX,{"derivedFrom":[subQ1,subQ0]});Q162=makeQuery(id+"F0.imprint","IMPRINT",FACE,{"disambiguationData":[TD([[makeQuery(id+"F0.imprint","IMPRINT",EDGE,{"disambiguationData":[TD([[subQ2,-1.0]])],"derivedFrom":subQ1}),-1.0]])]});}
            var Q163;
            {var subQ0=sQuery(id+"F0.wireOp",EDGE,"E33");var subQ1=sQuery(id+"F0.wireOp",EDGE,"E0.right");var subQ2=makeQuery(id+"F0.imprint","INTERSECT",VERTEX,{"derivedFrom":[subQ1,subQ0]});Q163=makeQuery(id+"F0.imprint","IMPRINT",FACE,{"disambiguationData":[TD([[makeQuery(id+"F0.imprint","IMPRINT",EDGE,{"disambiguationData":[TD([[subQ2,-1.0]])],"derivedFrom":subQ1}),-1.0]])]});}
            var Q164;
            {var subQ0=sQuery(id+"F0.wireOp",EDGE,"E28");var subQ1=sQuery(id+"F0.wireOp",EDGE,"E3");var subQ2=makeQuery(id+"F0.imprint","INTERSECT",VERTEX,{"derivedFrom":[subQ1,subQ0]});Q164=makeQuery(id+"F0.imprint","IMPRINT",FACE,{"disambiguationData":[TD([[makeQuery(id+"F0.imprint","IMPRINT",EDGE,{"disambiguationData":[TD([[subQ2,-1.0]])],"derivedFrom":subQ1}),1.0]])]});}
            var Q165;
            {var subQ0=sQuery(id+"F0.wireOp",EDGE,"E28");var subQ1=sQuery(id+"F0.wireOp",EDGE,"E6");var subQ2=makeQuery(id+"F0.imprint","INTERSECT",VERTEX,{"derivedFrom":[subQ1,subQ0]});Q165=makeQuery(id+"F0.imprint","IMPRINT",FACE,{"disambiguationData":[TD([[makeQuery(id+"F0.imprint","IMPRINT",EDGE,{"disambiguationData":[TD([[subQ2,-1.0]])],"derivedFrom":subQ1}),1.0]])]});}
            var Q166;
            {var subQ0=sQuery(id+"F0.wireOp",EDGE,"E28");var subQ1=sQuery(id+"F0.wireOp",EDGE,"E1");var subQ2=makeQuery(id+"F0.imprint","INTERSECT",VERTEX,{"derivedFrom":[subQ1,subQ0]});Q166=makeQuery(id+"F0.imprint","IMPRINT",FACE,{"disambiguationData":[TD([[makeQuery(id+"F0.imprint","IMPRINT",EDGE,{"disambiguationData":[TD([[subQ2,-1.0]])],"derivedFrom":subQ1}),1.0]])]});}
            var Q167;
            {var subQ0=sQuery(id+"F0.wireOp",EDGE,"E20");var subQ1=sQuery(id+"F0.wireOp",EDGE,"E10");var subQ2=makeQuery(id+"F0.imprint","INTERSECT",VERTEX,{"derivedFrom":[subQ1,subQ0]});Q167=makeQuery(id+"F0.imprint","IMPRINT",FACE,{"disambiguationData":[TD([[makeQuery(id+"F0.imprint","IMPRINT",EDGE,{"disambiguationData":[TD([[subQ2,-1.0]])],"derivedFrom":subQ1}),1.0]])]});}
            var Q168;
            {var subQ0=sQuery(id+"F0.wireOp",EDGE,"E20");var subQ1=sQuery(id+"F0.wireOp",EDGE,"E14");var subQ2=makeQuery(id+"F0.imprint","INTERSECT",VERTEX,{"derivedFrom":[subQ1,subQ0]});Q168=makeQuery(id+"F0.imprint","IMPRINT",FACE,{"disambiguationData":[TD([[makeQuery(id+"F0.imprint","IMPRINT",EDGE,{"disambiguationData":[TD([[subQ2,-1.0]])],"derivedFrom":subQ1}),1.0]])]});}
            var Q169;
            {var subQ0=sQuery(id+"F0.wireOp",EDGE,"E4");var subQ1=sQuery(id+"F0.wireOp",EDGE,"E0.bottom");var subQ2=makeQuery(id+"F0.imprint","INTERSECT",VERTEX,{"derivedFrom":[subQ1,subQ0]});Q169=makeQuery(id+"F0.imprint","IMPRINT",FACE,{"disambiguationData":[TD([[makeQuery(id+"F0.imprint","IMPRINT",EDGE,{"disambiguationData":[TD([[subQ2,-1.0]])],"derivedFrom":subQ1}),-1.0]])]});}
            var Q170;
            {var subQ0=sQuery(id+"F0.wireOp",EDGE,"E14");var subQ1=sQuery(id+"F0.wireOp",EDGE,"E0.bottom");var subQ2=makeQuery(id+"F0.imprint","INTERSECT",VERTEX,{"derivedFrom":[subQ1,subQ0]});Q170=makeQuery(id+"F0.imprint","IMPRINT",FACE,{"disambiguationData":[TD([[makeQuery(id+"F0.imprint","IMPRINT",EDGE,{"disambiguationData":[TD([[subQ2,-1.0]])],"derivedFrom":subQ1}),-1.0]])]});}
            var Q171;
            {var subQ0=sQuery(id+"F0.wireOp",EDGE,"E7");var subQ1=sQuery(id+"F0.wireOp",EDGE,"E0.top");var subQ2=makeQuery(id+"F0.imprint","INTERSECT",VERTEX,{"derivedFrom":[subQ1,subQ0]});Q171=makeQuery(id+"F0.imprint","IMPRINT",FACE,{"disambiguationData":[TD([[makeQuery(id+"F0.imprint","IMPRINT",EDGE,{"disambiguationData":[TD([[subQ2,-1.0]])],"derivedFrom":subQ1}),1.0]])]});}
            var Q172;
            {var subQ0=sQuery(id+"F0.wireOp",EDGE,"E30");var subQ1=sQuery(id+"F0.wireOp",EDGE,"E4");var subQ2=makeQuery(id+"F0.imprint","INTERSECT",VERTEX,{"derivedFrom":[subQ1,subQ0]});Q172=makeQuery(id+"F0.imprint","IMPRINT",FACE,{"disambiguationData":[TD([[makeQuery(id+"F0.imprint","IMPRINT",EDGE,{"disambiguationData":[TD([[subQ2,-1.0]])],"derivedFrom":subQ1}),1.0]])]});}
            var Q173;
            {var subQ0=sQuery(id+"F0.wireOp",EDGE,"E23");var subQ1=sQuery(id+"F0.wireOp",EDGE,"E0.right");var subQ2=makeQuery(id+"F0.imprint","INTERSECT",VERTEX,{"derivedFrom":[subQ1,subQ0]});Q173=makeQuery(id+"F0.imprint","IMPRINT",FACE,{"disambiguationData":[TD([[makeQuery(id+"F0.imprint","IMPRINT",EDGE,{"disambiguationData":[TD([[subQ2,-1.0]])],"derivedFrom":subQ1}),-1.0]])]});}
            var Q174;
            {var subQ0=sQuery(id+"F0.wireOp",EDGE,"E34");var subQ1=sQuery(id+"F0.wireOp",EDGE,"E16");var subQ2=makeQuery(id+"F0.imprint","INTERSECT",VERTEX,{"derivedFrom":[subQ1,subQ0]});Q174=makeQuery(id+"F0.imprint","IMPRINT",FACE,{"disambiguationData":[TD([[makeQuery(id+"F0.imprint","IMPRINT",EDGE,{"disambiguationData":[TD([[subQ2,-1.0]])],"derivedFrom":subQ1}),1.0]])]});}
            var Q175;
            {var subQ0=sQuery(id+"F0.wireOp",EDGE,"E32");var subQ1=sQuery(id+"F0.wireOp",EDGE,"E0.left");var subQ2=makeQuery(id+"F0.imprint","INTERSECT",VERTEX,{"derivedFrom":[subQ1,subQ0]});Q175=makeQuery(id+"F0.imprint","IMPRINT",FACE,{"disambiguationData":[TD([[makeQuery(id+"F0.imprint","IMPRINT",EDGE,{"disambiguationData":[TD([[subQ2,-1.0]])],"derivedFrom":subQ1}),1.0]])]});}
            var Q176;
            {var subQ0=sQuery(id+"F0.wireOp",EDGE,"E34");var subQ1=sQuery(id+"F0.wireOp",EDGE,"E7");var subQ2=makeQuery(id+"F0.imprint","INTERSECT",VERTEX,{"derivedFrom":[subQ1,subQ0]});Q176=makeQuery(id+"F0.imprint","IMPRINT",FACE,{"disambiguationData":[TD([[makeQuery(id+"F0.imprint","IMPRINT",EDGE,{"disambiguationData":[TD([[subQ2,-1.0]])],"derivedFrom":subQ1}),1.0]])]});}
            var Q177;
            {var subQ0=sQuery(id+"F0.wireOp",EDGE,"E22");var subQ1=sQuery(id+"F0.wireOp",EDGE,"E4");var subQ2=makeQuery(id+"F0.imprint","INTERSECT",VERTEX,{"derivedFrom":[subQ1,subQ0]});Q177=makeQuery(id+"F0.imprint","IMPRINT",FACE,{"disambiguationData":[TD([[makeQuery(id+"F0.imprint","IMPRINT",EDGE,{"disambiguationData":[TD([[subQ2,-1.0]])],"derivedFrom":subQ1}),1.0]])]});}
            var Q178;
            {var subQ0=sQuery(id+"F0.wireOp",EDGE,"E14");var subQ1=sQuery(id+"F0.wireOp",EDGE,"E0.top");var subQ2=makeQuery(id+"F0.imprint","INTERSECT",VERTEX,{"derivedFrom":[subQ1,subQ0]});Q178=makeQuery(id+"F0.imprint","IMPRINT",FACE,{"disambiguationData":[TD([[makeQuery(id+"F0.imprint","IMPRINT",EDGE,{"disambiguationData":[TD([[subQ2,-1.0]])],"derivedFrom":subQ1}),1.0]])]});}
            var Q179;
            {var subQ0=sQuery(id+"F0.wireOp",EDGE,"E34");var subQ1=sQuery(id+"F0.wireOp",EDGE,"E1");var subQ2=makeQuery(id+"F0.imprint","INTERSECT",VERTEX,{"derivedFrom":[subQ1,subQ0]});Q179=makeQuery(id+"F0.imprint","IMPRINT",FACE,{"disambiguationData":[TD([[makeQuery(id+"F0.imprint","IMPRINT",EDGE,{"disambiguationData":[TD([[subQ2,-1.0]])],"derivedFrom":subQ1}),1.0]])]});}
            var Q180;
            {var subQ0=sQuery(id+"F0.wireOp",EDGE,"E21");var subQ1=sQuery(id+"F0.wireOp",EDGE,"E0.right");var subQ2=makeQuery(id+"F0.imprint","INTERSECT",VERTEX,{"derivedFrom":[subQ1,subQ0]});Q180=makeQuery(id+"F0.imprint","IMPRINT",FACE,{"disambiguationData":[TD([[makeQuery(id+"F0.imprint","IMPRINT",EDGE,{"disambiguationData":[TD([[subQ2,-1.0]])],"derivedFrom":subQ1}),-1.0]])]});}
            var Q181;
            {var subQ0=sQuery(id+"F0.wireOp",EDGE,"E16");var subQ1=sQuery(id+"F0.wireOp",EDGE,"E0.top");var subQ2=makeQuery(id+"F0.imprint","INTERSECT",VERTEX,{"derivedFrom":[subQ1,subQ0]});Q181=makeQuery(id+"F0.imprint","IMPRINT",FACE,{"disambiguationData":[TD([[makeQuery(id+"F0.imprint","IMPRINT",EDGE,{"disambiguationData":[TD([[subQ2,-1.0]])],"derivedFrom":subQ1}),1.0]])]});}
            var Q182;
            {var subQ0=sQuery(id+"F0.wireOp",EDGE,"E31");var subQ1=sQuery(id+"F0.wireOp",EDGE,"E4");var subQ2=makeQuery(id+"F0.imprint","INTERSECT",VERTEX,{"derivedFrom":[subQ1,subQ0]});Q182=makeQuery(id+"F0.imprint","IMPRINT",FACE,{"disambiguationData":[TD([[makeQuery(id+"F0.imprint","IMPRINT",EDGE,{"disambiguationData":[TD([[subQ2,-1.0]])],"derivedFrom":subQ1}),1.0]])]});}
            var Q183;
            {var subQ0=sQuery(id+"F0.wireOp",EDGE,"E32");var subQ1=sQuery(id+"F0.wireOp",EDGE,"E4");var subQ2=makeQuery(id+"F0.imprint","INTERSECT",VERTEX,{"derivedFrom":[subQ1,subQ0]});Q183=makeQuery(id+"F0.imprint","IMPRINT",FACE,{"disambiguationData":[TD([[makeQuery(id+"F0.imprint","IMPRINT",EDGE,{"disambiguationData":[TD([[subQ2,-1.0]])],"derivedFrom":subQ1}),1.0]])]});}
            var Q184;
            {var subQ0=sQuery(id+"F0.wireOp",EDGE,"E33");var subQ1=sQuery(id+"F0.wireOp",EDGE,"E0.left");var subQ2=makeQuery(id+"F0.imprint","INTERSECT",VERTEX,{"derivedFrom":[subQ1,subQ0]});Q184=makeQuery(id+"F0.imprint","IMPRINT",FACE,{"disambiguationData":[TD([[makeQuery(id+"F0.imprint","IMPRINT",EDGE,{"disambiguationData":[TD([[subQ2,-1.0]])],"derivedFrom":subQ1}),1.0]])]});}
            var Q185;
            {var subQ0=sQuery(id+"F0.wireOp",EDGE,"E20");var subQ1=sQuery(id+"F0.wireOp",EDGE,"E3");var subQ2=makeQuery(id+"F0.imprint","INTERSECT",VERTEX,{"derivedFrom":[subQ1,subQ0]});Q185=makeQuery(id+"F0.imprint","IMPRINT",FACE,{"disambiguationData":[TD([[makeQuery(id+"F0.imprint","IMPRINT",EDGE,{"disambiguationData":[TD([[subQ2,-1.0]])],"derivedFrom":subQ1}),1.0]])]});}
            var Q186;
            {var subQ0=sQuery(id+"F0.wireOp",EDGE,"E20");var subQ1=sQuery(id+"F0.wireOp",EDGE,"E17");var subQ2=makeQuery(id+"F0.imprint","INTERSECT",VERTEX,{"derivedFrom":[subQ1,subQ0]});Q186=makeQuery(id+"F0.imprint","IMPRINT",FACE,{"disambiguationData":[TD([[makeQuery(id+"F0.imprint","IMPRINT",EDGE,{"disambiguationData":[TD([[subQ2,-1.0]])],"derivedFrom":subQ1}),1.0]])]});}
            var Q187;
            {var subQ0=sQuery(id+"F0.wireOp",EDGE,"E28");var subQ1=sQuery(id+"F0.wireOp",EDGE,"E13");var subQ2=makeQuery(id+"F0.imprint","INTERSECT",VERTEX,{"derivedFrom":[subQ1,subQ0]});Q187=makeQuery(id+"F0.imprint","IMPRINT",FACE,{"disambiguationData":[TD([[makeQuery(id+"F0.imprint","IMPRINT",EDGE,{"disambiguationData":[TD([[subQ2,-1.0]])],"derivedFrom":subQ1}),1.0]])]});}
            var Q188;
            {var subQ0=sQuery(id+"F0.wireOp",EDGE,"E35");var subQ1=sQuery(id+"F0.wireOp",EDGE,"E4");var subQ2=makeQuery(id+"F0.imprint","INTERSECT",VERTEX,{"derivedFrom":[subQ1,subQ0]});Q188=makeQuery(id+"F0.imprint","IMPRINT",FACE,{"disambiguationData":[TD([[makeQuery(id+"F0.imprint","IMPRINT",EDGE,{"disambiguationData":[TD([[subQ2,-1.0]])],"derivedFrom":subQ1}),1.0]])]});}
            var Q189;
            {var subQ0=sQuery(id+"F0.wireOp",EDGE,"E34");var subQ1=sQuery(id+"F0.wireOp",EDGE,"E11");var subQ2=makeQuery(id+"F0.imprint","INTERSECT",VERTEX,{"derivedFrom":[subQ1,subQ0]});Q189=makeQuery(id+"F0.imprint","IMPRINT",FACE,{"disambiguationData":[TD([[makeQuery(id+"F0.imprint","IMPRINT",EDGE,{"disambiguationData":[TD([[subQ2,-1.0]])],"derivedFrom":subQ1}),1.0]])]});}
            var Q190;
            {var subQ0=sQuery(id+"F0.wireOp",EDGE,"E11");var subQ1=sQuery(id+"F0.wireOp",EDGE,"E0.bottom");var subQ2=makeQuery(id+"F0.imprint","INTERSECT",VERTEX,{"derivedFrom":[subQ1,subQ0]});Q190=makeQuery(id+"F0.imprint","IMPRINT",FACE,{"disambiguationData":[TD([[makeQuery(id+"F0.imprint","IMPRINT",EDGE,{"disambiguationData":[TD([[subQ2,-1.0]])],"derivedFrom":subQ1}),-1.0]])]});}
            var Q191;
            {var subQ0=sQuery(id+"F0.wireOp",EDGE,"E23");var subQ1=sQuery(id+"F0.wireOp",EDGE,"E0.left");var subQ2=makeQuery(id+"F0.imprint","INTERSECT",VERTEX,{"derivedFrom":[subQ1,subQ0]});Q191=makeQuery(id+"F0.imprint","IMPRINT",FACE,{"disambiguationData":[TD([[makeQuery(id+"F0.imprint","IMPRINT",EDGE,{"disambiguationData":[TD([[subQ2,-1.0]])],"derivedFrom":subQ1}),1.0]])]});}
            var Q192;
            {var subQ0=sQuery(id+"F0.wireOp",EDGE,"E26");var subQ1=sQuery(id+"F0.wireOp",EDGE,"E0.left");var subQ2=makeQuery(id+"F0.imprint","INTERSECT",VERTEX,{"derivedFrom":[subQ1,subQ0]});Q192=makeQuery(id+"F0.imprint","IMPRINT",FACE,{"disambiguationData":[TD([[makeQuery(id+"F0.imprint","IMPRINT",EDGE,{"disambiguationData":[TD([[subQ2,-1.0]])],"derivedFrom":subQ1}),1.0]])]});}
            var Q193;
            {var subQ0=sQuery(id+"F0.wireOp",EDGE,"E24");var subQ1=sQuery(id+"F0.wireOp",EDGE,"E0.left");var subQ2=makeQuery(id+"F0.imprint","INTERSECT",VERTEX,{"derivedFrom":[subQ1,subQ0]});Q193=makeQuery(id+"F0.imprint","IMPRINT",FACE,{"disambiguationData":[TD([[makeQuery(id+"F0.imprint","IMPRINT",EDGE,{"disambiguationData":[TD([[subQ2,-1.0]])],"derivedFrom":subQ1}),1.0]])]});}
            var Q194;
            {var subQ0=sQuery(id+"F0.wireOp",EDGE,"E31");var subQ1=sQuery(id+"F0.wireOp",EDGE,"E0.left");var subQ2=makeQuery(id+"F0.imprint","INTERSECT",VERTEX,{"derivedFrom":[subQ1,subQ0]});Q194=makeQuery(id+"F0.imprint","IMPRINT",FACE,{"disambiguationData":[TD([[makeQuery(id+"F0.imprint","IMPRINT",EDGE,{"disambiguationData":[TD([[subQ2,-1.0]])],"derivedFrom":subQ1}),1.0]])]});}
            var Q195;
            {var subQ0=sQuery(id+"F0.wireOp",EDGE,"E20");var subQ1=sQuery(id+"F0.wireOp",EDGE,"E0.right");var subQ2=makeQuery(id+"F0.imprint","INTERSECT",VERTEX,{"derivedFrom":[subQ1,subQ0]});Q195=makeQuery(id+"F0.imprint","IMPRINT",FACE,{"disambiguationData":[TD([[makeQuery(id+"F0.imprint","IMPRINT",EDGE,{"disambiguationData":[TD([[subQ2,-1.0]])],"derivedFrom":subQ1}),-1.0]])]});}
            var Q196;
            {var subQ0=sQuery(id+"F0.wireOp",EDGE,"E8");var subQ1=sQuery(id+"F0.wireOp",EDGE,"E0.bottom");var subQ2=makeQuery(id+"F0.imprint","INTERSECT",VERTEX,{"derivedFrom":[subQ1,subQ0]});Q196=makeQuery(id+"F0.imprint","IMPRINT",FACE,{"disambiguationData":[TD([[makeQuery(id+"F0.imprint","IMPRINT",EDGE,{"disambiguationData":[TD([[subQ2,-1.0]])],"derivedFrom":subQ1}),-1.0]])]});}
            var Q197;
            {var subQ0=sQuery(id+"F0.wireOp",EDGE,"E30");var subQ1=sQuery(id+"F0.wireOp",EDGE,"E0.right");var subQ2=makeQuery(id+"F0.imprint","INTERSECT",VERTEX,{"derivedFrom":[subQ1,subQ0]});Q197=makeQuery(id+"F0.imprint","IMPRINT",FACE,{"disambiguationData":[TD([[makeQuery(id+"F0.imprint","IMPRINT",EDGE,{"disambiguationData":[TD([[subQ2,-1.0]])],"derivedFrom":subQ1}),-1.0]])]});}
            var Q198;
            {var subQ0=sQuery(id+"F0.wireOp",EDGE,"E20");var subQ1=sQuery(id+"F0.wireOp",EDGE,"E9");var subQ2=makeQuery(id+"F0.imprint","INTERSECT",VERTEX,{"derivedFrom":[subQ1,subQ0]});Q198=makeQuery(id+"F0.imprint","IMPRINT",FACE,{"disambiguationData":[TD([[makeQuery(id+"F0.imprint","IMPRINT",EDGE,{"disambiguationData":[TD([[subQ2,-1.0]])],"derivedFrom":subQ1}),1.0]])]});}
            var Q199;
            {var subQ0=sQuery(id+"F0.wireOp",EDGE,"E20");var subQ1=sQuery(id+"F0.wireOp",EDGE,"E4");var subQ2=makeQuery(id+"F0.imprint","INTERSECT",VERTEX,{"derivedFrom":[subQ1,subQ0]});Q199=makeQuery(id+"F0.imprint","IMPRINT",FACE,{"disambiguationData":[TD([[makeQuery(id+"F0.imprint","IMPRINT",EDGE,{"disambiguationData":[TD([[subQ2,-1.0]])],"derivedFrom":subQ1}),1.0]])]});}
            var Q200;
            {var subQ0=sQuery(id+"F0.wireOp",EDGE,"E19");var subQ1=sQuery(id+"F0.wireOp",EDGE,"E0.left");var subQ2=makeQuery(id+"F0.imprint","INTERSECT",VERTEX,{"derivedFrom":[subQ1,subQ0]});Q200=makeQuery(id+"F0.imprint","IMPRINT",FACE,{"disambiguationData":[TD([[makeQuery(id+"F0.imprint","IMPRINT",EDGE,{"disambiguationData":[TD([[subQ2,-1.0]])],"derivedFrom":subQ1}),1.0]])]});}
            var Q201;
            {var subQ0=sQuery(id+"F0.wireOp",EDGE,"E22");var subQ1=sQuery(id+"F0.wireOp",EDGE,"E0.left");var subQ2=makeQuery(id+"F0.imprint","INTERSECT",VERTEX,{"derivedFrom":[subQ1,subQ0]});Q201=makeQuery(id+"F0.imprint","IMPRINT",FACE,{"disambiguationData":[TD([[makeQuery(id+"F0.imprint","IMPRINT",EDGE,{"disambiguationData":[TD([[subQ2,-1.0]])],"derivedFrom":subQ1}),1.0]])]});}
            var Q202;
            {var subQ0=sQuery(id+"F0.wireOp",EDGE,"E34");var subQ1=sQuery(id+"F0.wireOp",EDGE,"E0.left");var subQ2=makeQuery(id+"F0.imprint","INTERSECT",VERTEX,{"derivedFrom":[subQ1,subQ0]});Q202=makeQuery(id+"F0.imprint","IMPRINT",FACE,{"disambiguationData":[TD([[makeQuery(id+"F0.imprint","IMPRINT",EDGE,{"disambiguationData":[TD([[subQ2,-1.0]])],"derivedFrom":subQ1}),1.0]])]});}
            var Q203;
            {var subQ0=sQuery(id+"F0.wireOp",EDGE,"E34");var subQ1=sQuery(id+"F0.wireOp",EDGE,"E10");var subQ2=makeQuery(id+"F0.imprint","INTERSECT",VERTEX,{"derivedFrom":[subQ1,subQ0]});Q203=makeQuery(id+"F0.imprint","IMPRINT",FACE,{"disambiguationData":[TD([[makeQuery(id+"F0.imprint","IMPRINT",EDGE,{"disambiguationData":[TD([[subQ2,-1.0]])],"derivedFrom":subQ1}),1.0]])]});}
            var Q204;
            {var subQ0=sQuery(id+"F0.wireOp",EDGE,"E20");var subQ1=sQuery(id+"F0.wireOp",EDGE,"E8");var subQ2=makeQuery(id+"F0.imprint","INTERSECT",VERTEX,{"derivedFrom":[subQ1,subQ0]});Q204=makeQuery(id+"F0.imprint","IMPRINT",FACE,{"disambiguationData":[TD([[makeQuery(id+"F0.imprint","IMPRINT",EDGE,{"disambiguationData":[TD([[subQ2,-1.0]])],"derivedFrom":subQ1}),1.0]])]});}
            var Q205;
            {var subQ0=sQuery(id+"F0.wireOp",EDGE,"E25");var subQ1=sQuery(id+"F0.wireOp",EDGE,"E0.left");var subQ2=makeQuery(id+"F0.imprint","INTERSECT",VERTEX,{"derivedFrom":[subQ1,subQ0]});Q205=makeQuery(id+"F0.imprint","IMPRINT",FACE,{"disambiguationData":[TD([[makeQuery(id+"F0.imprint","IMPRINT",EDGE,{"disambiguationData":[TD([[subQ2,-1.0]])],"derivedFrom":subQ1}),1.0]])]});}
            var Q206;
            {var subQ0=sQuery(id+"F0.wireOp",EDGE,"E26");var subQ1=sQuery(id+"F0.wireOp",EDGE,"E0.right");var subQ2=makeQuery(id+"F0.imprint","INTERSECT",VERTEX,{"derivedFrom":[subQ1,subQ0]});Q206=makeQuery(id+"F0.imprint","IMPRINT",FACE,{"disambiguationData":[TD([[makeQuery(id+"F0.imprint","IMPRINT",EDGE,{"disambiguationData":[TD([[subQ2,-1.0]])],"derivedFrom":subQ1}),-1.0]])]});}
            var Q207;
            {var subQ0=sQuery(id+"F0.wireOp",EDGE,"E20");var subQ1=sQuery(id+"F0.wireOp",EDGE,"E11");var subQ2=makeQuery(id+"F0.imprint","INTERSECT",VERTEX,{"derivedFrom":[subQ1,subQ0]});Q207=makeQuery(id+"F0.imprint","IMPRINT",FACE,{"disambiguationData":[TD([[makeQuery(id+"F0.imprint","IMPRINT",EDGE,{"disambiguationData":[TD([[subQ2,-1.0]])],"derivedFrom":subQ1}),1.0]])]});}
            var Q208;
            {var subQ0=sQuery(id+"F0.wireOp",EDGE,"E34");var subQ1=sQuery(id+"F0.wireOp",EDGE,"E12");var subQ2=makeQuery(id+"F0.imprint","INTERSECT",VERTEX,{"derivedFrom":[subQ1,subQ0]});Q208=makeQuery(id+"F0.imprint","IMPRINT",FACE,{"disambiguationData":[TD([[makeQuery(id+"F0.imprint","IMPRINT",EDGE,{"disambiguationData":[TD([[subQ2,-1.0]])],"derivedFrom":subQ1}),1.0]])]});}
            var Q209;
            {var subQ0=sQuery(id+"F0.wireOp",EDGE,"E1");var subQ1=sQuery(id+"F0.wireOp",EDGE,"E0.top");var subQ2=makeQuery(id+"F0.imprint","INTERSECT",VERTEX,{"derivedFrom":[subQ1,subQ0]});Q209=makeQuery(id+"F0.imprint","IMPRINT",FACE,{"disambiguationData":[TD([[makeQuery(id+"F0.imprint","IMPRINT",EDGE,{"disambiguationData":[TD([[subQ2,-1.0]])],"derivedFrom":subQ1}),1.0]])]});}
            var Q210;
            {var subQ0=sQuery(id+"F0.wireOp",EDGE,"E8");var subQ1=sQuery(id+"F0.wireOp",EDGE,"E0.top");var subQ2=makeQuery(id+"F0.imprint","INTERSECT",VERTEX,{"derivedFrom":[subQ1,subQ0]});Q210=makeQuery(id+"F0.imprint","IMPRINT",FACE,{"disambiguationData":[TD([[makeQuery(id+"F0.imprint","IMPRINT",EDGE,{"disambiguationData":[TD([[subQ2,-1.0]])],"derivedFrom":subQ1}),1.0]])]});}
            var Q211;
            {var subQ0=sQuery(id+"F0.wireOp",EDGE,"E34");var subQ1=sQuery(id+"F0.wireOp",EDGE,"E8");var subQ2=makeQuery(id+"F0.imprint","INTERSECT",VERTEX,{"derivedFrom":[subQ1,subQ0]});Q211=makeQuery(id+"F0.imprint","IMPRINT",FACE,{"disambiguationData":[TD([[makeQuery(id+"F0.imprint","IMPRINT",EDGE,{"disambiguationData":[TD([[subQ2,-1.0]])],"derivedFrom":subQ1}),1.0]])]});}
            var Q212;
            {var subQ0=sQuery(id+"F0.wireOp",EDGE,"E29");var subQ1=sQuery(id+"F0.wireOp",EDGE,"E0.right");var subQ2=makeQuery(id+"F0.imprint","INTERSECT",VERTEX,{"derivedFrom":[subQ1,subQ0]});Q212=makeQuery(id+"F0.imprint","IMPRINT",FACE,{"disambiguationData":[TD([[makeQuery(id+"F0.imprint","IMPRINT",EDGE,{"disambiguationData":[TD([[subQ2,-1.0]])],"derivedFrom":subQ1}),-1.0]])]});}
            var Q213;
            {var subQ0=sQuery(id+"F0.wireOp",EDGE,"E28");var subQ1=sQuery(id+"F0.wireOp",EDGE,"E17");var subQ2=makeQuery(id+"F0.imprint","INTERSECT",VERTEX,{"derivedFrom":[subQ1,subQ0]});Q213=makeQuery(id+"F0.imprint","IMPRINT",FACE,{"disambiguationData":[TD([[makeQuery(id+"F0.imprint","IMPRINT",EDGE,{"disambiguationData":[TD([[subQ2,-1.0]])],"derivedFrom":subQ1}),1.0]])]});}
            var Q214;
            {var subQ0=sQuery(id+"F0.wireOp",EDGE,"E34");var subQ1=sQuery(id+"F0.wireOp",EDGE,"E2");var subQ2=makeQuery(id+"F0.imprint","INTERSECT",VERTEX,{"derivedFrom":[subQ1,subQ0]});Q214=makeQuery(id+"F0.imprint","IMPRINT",FACE,{"disambiguationData":[TD([[makeQuery(id+"F0.imprint","IMPRINT",EDGE,{"disambiguationData":[TD([[subQ2,-1.0]])],"derivedFrom":subQ1}),1.0]])]});}
            var Q215;
            {var subQ0=sQuery(id+"F0.wireOp",EDGE,"E15");var subQ1=sQuery(id+"F0.wireOp",EDGE,"E0.bottom");var subQ2=makeQuery(id+"F0.imprint","INTERSECT",VERTEX,{"derivedFrom":[subQ1,subQ0]});Q215=makeQuery(id+"F0.imprint","IMPRINT",FACE,{"disambiguationData":[TD([[makeQuery(id+"F0.imprint","IMPRINT",EDGE,{"disambiguationData":[TD([[subQ2,-1.0]])],"derivedFrom":subQ1}),-1.0]])]});}
            var Q216;
            {var subQ0=sQuery(id+"F0.wireOp",EDGE,"E28");var subQ1=sQuery(id+"F0.wireOp",EDGE,"E9");var subQ2=makeQuery(id+"F0.imprint","INTERSECT",VERTEX,{"derivedFrom":[subQ1,subQ0]});Q216=makeQuery(id+"F0.imprint","IMPRINT",FACE,{"disambiguationData":[TD([[makeQuery(id+"F0.imprint","IMPRINT",EDGE,{"disambiguationData":[TD([[subQ2,-1.0]])],"derivedFrom":subQ1}),1.0]])]});}
            var Q217;
            {var subQ0=sQuery(id+"F0.wireOp",EDGE,"E5");var subQ1=sQuery(id+"F0.wireOp",EDGE,"E0.bottom");var subQ2=makeQuery(id+"F0.imprint","INTERSECT",VERTEX,{"derivedFrom":[subQ1,subQ0]});Q217=makeQuery(id+"F0.imprint","IMPRINT",FACE,{"disambiguationData":[TD([[makeQuery(id+"F0.imprint","IMPRINT",EDGE,{"disambiguationData":[TD([[subQ2,-1.0]])],"derivedFrom":subQ1}),-1.0]])]});}
            var Q218;
            {var subQ0=sQuery(id+"F0.wireOp",EDGE,"E2");var subQ1=sQuery(id+"F0.wireOp",EDGE,"E0.bottom");var subQ2=makeQuery(id+"F0.imprint","INTERSECT",VERTEX,{"derivedFrom":[subQ1,subQ0]});Q218=makeQuery(id+"F0.imprint","IMPRINT",FACE,{"disambiguationData":[TD([[makeQuery(id+"F0.imprint","IMPRINT",EDGE,{"disambiguationData":[TD([[subQ2,-1.0]])],"derivedFrom":subQ1}),-1.0]])]});}
            var Q219;
            {var subQ0=sQuery(id+"F0.wireOp",EDGE,"E34");var subQ1=sQuery(id+"F0.wireOp",EDGE,"E14");var subQ2=makeQuery(id+"F0.imprint","INTERSECT",VERTEX,{"derivedFrom":[subQ1,subQ0]});Q219=makeQuery(id+"F0.imprint","IMPRINT",FACE,{"disambiguationData":[TD([[makeQuery(id+"F0.imprint","IMPRINT",EDGE,{"disambiguationData":[TD([[subQ2,-1.0]])],"derivedFrom":subQ1}),1.0]])]});}
            var Q220;
            {var subQ0=sQuery(id+"F0.wireOp",EDGE,"E3");var subQ1=sQuery(id+"F0.wireOp",EDGE,"E0.bottom");var subQ2=makeQuery(id+"F0.imprint","INTERSECT",VERTEX,{"derivedFrom":[subQ1,subQ0]});Q220=makeQuery(id+"F0.imprint","IMPRINT",FACE,{"disambiguationData":[TD([[makeQuery(id+"F0.imprint","IMPRINT",EDGE,{"disambiguationData":[TD([[subQ2,-1.0]])],"derivedFrom":subQ1}),-1.0]])]});}
            var Q221;
            {var subQ0=sQuery(id+"F0.wireOp",EDGE,"E28");var subQ1=sQuery(id+"F0.wireOp",EDGE,"E7");var subQ2=makeQuery(id+"F0.imprint","INTERSECT",VERTEX,{"derivedFrom":[subQ1,subQ0]});Q221=makeQuery(id+"F0.imprint","IMPRINT",FACE,{"disambiguationData":[TD([[makeQuery(id+"F0.imprint","IMPRINT",EDGE,{"disambiguationData":[TD([[subQ2,-1.0]])],"derivedFrom":subQ1}),1.0]])]});}
            var Q222;
            {var subQ0=sQuery(id+"F0.wireOp",EDGE,"E34");var subQ1=sQuery(id+"F0.wireOp",EDGE,"E9");var subQ2=makeQuery(id+"F0.imprint","INTERSECT",VERTEX,{"derivedFrom":[subQ1,subQ0]});Q222=makeQuery(id+"F0.imprint","IMPRINT",FACE,{"disambiguationData":[TD([[makeQuery(id+"F0.imprint","IMPRINT",EDGE,{"disambiguationData":[TD([[subQ2,-1.0]])],"derivedFrom":subQ1}),1.0]])]});}
            var Q223;
            {var subQ0=sQuery(id+"F0.wireOp",EDGE,"E13");var subQ1=sQuery(id+"F0.wireOp",EDGE,"E0.top");var subQ2=makeQuery(id+"F0.imprint","INTERSECT",VERTEX,{"derivedFrom":[subQ1,subQ0]});Q223=makeQuery(id+"F0.imprint","IMPRINT",FACE,{"disambiguationData":[TD([[makeQuery(id+"F0.imprint","IMPRINT",EDGE,{"disambiguationData":[TD([[subQ2,-1.0]])],"derivedFrom":subQ1}),1.0]])]});}
            var Q224;
            {var subQ0=sQuery(id+"F0.wireOp",EDGE,"E28");var subQ1=sQuery(id+"F0.wireOp",EDGE,"E0.left");var subQ2=makeQuery(id+"F0.imprint","INTERSECT",VERTEX,{"derivedFrom":[subQ1,subQ0]});Q224=makeQuery(id+"F0.imprint","IMPRINT",FACE,{"disambiguationData":[TD([[makeQuery(id+"F0.imprint","IMPRINT",EDGE,{"disambiguationData":[TD([[subQ2,-1.0]])],"derivedFrom":subQ1}),1.0]])]});}
            var Q225;
            {var subQ0=sQuery(id+"F0.wireOp",EDGE,"E29");var subQ1=sQuery(id+"F0.wireOp",EDGE,"E4");var subQ2=makeQuery(id+"F0.imprint","INTERSECT",VERTEX,{"derivedFrom":[subQ1,subQ0]});Q225=makeQuery(id+"F0.imprint","IMPRINT",FACE,{"disambiguationData":[TD([[makeQuery(id+"F0.imprint","IMPRINT",EDGE,{"disambiguationData":[TD([[subQ2,-1.0]])],"derivedFrom":subQ1}),1.0]])]});}
            var Q226;
            {var subQ0=sQuery(id+"F0.wireOp",EDGE,"E20");var subQ1=sQuery(id+"F0.wireOp",EDGE,"E2");var subQ2=makeQuery(id+"F0.imprint","INTERSECT",VERTEX,{"derivedFrom":[subQ1,subQ0]});Q226=makeQuery(id+"F0.imprint","IMPRINT",FACE,{"disambiguationData":[TD([[makeQuery(id+"F0.imprint","IMPRINT",EDGE,{"disambiguationData":[TD([[subQ2,-1.0]])],"derivedFrom":subQ1}),1.0]])]});}
            var Q227;
            {var subQ0=sQuery(id+"F0.wireOp",EDGE,"E27");var subQ1=sQuery(id+"F0.wireOp",EDGE,"E4");var subQ2=makeQuery(id+"F0.imprint","INTERSECT",VERTEX,{"derivedFrom":[subQ1,subQ0]});Q227=makeQuery(id+"F0.imprint","IMPRINT",FACE,{"disambiguationData":[TD([[makeQuery(id+"F0.imprint","IMPRINT",EDGE,{"disambiguationData":[TD([[subQ2,-1.0]])],"derivedFrom":subQ1}),1.0]])]});}
            var Q228;
            {var subQ0=sQuery(id+"F0.wireOp",EDGE,"E10");var subQ1=sQuery(id+"F0.wireOp",EDGE,"E0.top");var subQ2=makeQuery(id+"F0.imprint","INTERSECT",VERTEX,{"derivedFrom":[subQ1,subQ0]});Q228=makeQuery(id+"F0.imprint","IMPRINT",FACE,{"disambiguationData":[TD([[makeQuery(id+"F0.imprint","IMPRINT",EDGE,{"disambiguationData":[TD([[subQ2,-1.0]])],"derivedFrom":subQ1}),1.0]])]});}
            var Q229;
            {var subQ0=sQuery(id+"F0.wireOp",EDGE,"E21");var subQ1=sQuery(id+"F0.wireOp",EDGE,"E0.left");var subQ2=makeQuery(id+"F0.imprint","INTERSECT",VERTEX,{"derivedFrom":[subQ1,subQ0]});Q229=makeQuery(id+"F0.imprint","IMPRINT",FACE,{"disambiguationData":[TD([[makeQuery(id+"F0.imprint","IMPRINT",EDGE,{"disambiguationData":[TD([[subQ2,-1.0]])],"derivedFrom":subQ1}),1.0]])]});}
            var Q230;
            {var subQ0=sQuery(id+"F0.wireOp",EDGE,"E28");var subQ1=sQuery(id+"F0.wireOp",EDGE,"E15");var subQ2=makeQuery(id+"F0.imprint","INTERSECT",VERTEX,{"derivedFrom":[subQ1,subQ0]});Q230=makeQuery(id+"F0.imprint","IMPRINT",FACE,{"disambiguationData":[TD([[makeQuery(id+"F0.imprint","IMPRINT",EDGE,{"disambiguationData":[TD([[subQ2,-1.0]])],"derivedFrom":subQ1}),1.0]])]});}
            var Q231;
            {var subQ0=sQuery(id+"F0.wireOp",EDGE,"E9");var subQ1=sQuery(id+"F0.wireOp",EDGE,"E0.top");var subQ2=makeQuery(id+"F0.imprint","INTERSECT",VERTEX,{"derivedFrom":[subQ1,subQ0]});Q231=makeQuery(id+"F0.imprint","IMPRINT",FACE,{"disambiguationData":[TD([[makeQuery(id+"F0.imprint","IMPRINT",EDGE,{"disambiguationData":[TD([[subQ2,-1.0]])],"derivedFrom":subQ1}),1.0]])]});}
            var Q232;
            {var subQ0=sQuery(id+"F0.wireOp",EDGE,"E34");var subQ1=sQuery(id+"F0.wireOp",EDGE,"E13");var subQ2=makeQuery(id+"F0.imprint","INTERSECT",VERTEX,{"derivedFrom":[subQ1,subQ0]});Q232=makeQuery(id+"F0.imprint","IMPRINT",FACE,{"disambiguationData":[TD([[makeQuery(id+"F0.imprint","IMPRINT",EDGE,{"disambiguationData":[TD([[subQ2,-1.0]])],"derivedFrom":subQ1}),1.0]])]});}
            var Q233;
            {var subQ0=sQuery(id+"F0.wireOp",EDGE,"E29");var subQ1=sQuery(id+"F0.wireOp",EDGE,"E0.left");var subQ2=makeQuery(id+"F0.imprint","INTERSECT",VERTEX,{"derivedFrom":[subQ1,subQ0]});Q233=makeQuery(id+"F0.imprint","IMPRINT",FACE,{"disambiguationData":[TD([[makeQuery(id+"F0.imprint","IMPRINT",EDGE,{"disambiguationData":[TD([[subQ2,-1.0]])],"derivedFrom":subQ1}),1.0]])]});}
            var Q234;
            {var subQ0=sQuery(id+"F0.wireOp",EDGE,"E31");var subQ1=sQuery(id+"F0.wireOp",EDGE,"E0.right");var subQ2=makeQuery(id+"F0.imprint","INTERSECT",VERTEX,{"derivedFrom":[subQ1,subQ0]});Q234=makeQuery(id+"F0.imprint","IMPRINT",FACE,{"disambiguationData":[TD([[makeQuery(id+"F0.imprint","IMPRINT",EDGE,{"disambiguationData":[TD([[subQ2,-1.0]])],"derivedFrom":subQ1}),-1.0]])]});}
            var Q235;
            {var subQ0=sQuery(id+"F0.wireOp",EDGE,"E11");var subQ1=sQuery(id+"F0.wireOp",EDGE,"E0.top");var subQ2=makeQuery(id+"F0.imprint","INTERSECT",VERTEX,{"derivedFrom":[subQ1,subQ0]});Q235=makeQuery(id+"F0.imprint","IMPRINT",FACE,{"disambiguationData":[TD([[makeQuery(id+"F0.imprint","IMPRINT",EDGE,{"disambiguationData":[TD([[subQ2,-1.0]])],"derivedFrom":subQ1}),1.0]])]});}
            var Q236;
            {var subQ0=sQuery(id+"F0.wireOp",EDGE,"E4");var subQ1=sQuery(id+"F0.wireOp",EDGE,"E0.top");var subQ2=makeQuery(id+"F0.imprint","INTERSECT",VERTEX,{"derivedFrom":[subQ1,subQ0]});Q236=makeQuery(id+"F0.imprint","IMPRINT",FACE,{"disambiguationData":[TD([[makeQuery(id+"F0.imprint","IMPRINT",EDGE,{"disambiguationData":[TD([[subQ2,-1.0]])],"derivedFrom":subQ1}),1.0]])]});}
            var Q237;
            {var subQ0=sQuery(id+"F0.wireOp",EDGE,"E12");var subQ1=sQuery(id+"F0.wireOp",EDGE,"E0.top");var subQ2=makeQuery(id+"F0.imprint","INTERSECT",VERTEX,{"derivedFrom":[subQ1,subQ0]});Q237=makeQuery(id+"F0.imprint","IMPRINT",FACE,{"disambiguationData":[TD([[makeQuery(id+"F0.imprint","IMPRINT",EDGE,{"disambiguationData":[TD([[subQ2,-1.0]])],"derivedFrom":subQ1}),1.0]])]});}
            var Q238;
            {var subQ0=sQuery(id+"F0.wireOp",EDGE,"E28");var subQ1=sQuery(id+"F0.wireOp",EDGE,"E8");var subQ2=makeQuery(id+"F0.imprint","INTERSECT",VERTEX,{"derivedFrom":[subQ1,subQ0]});Q238=makeQuery(id+"F0.imprint","IMPRINT",FACE,{"disambiguationData":[TD([[makeQuery(id+"F0.imprint","IMPRINT",EDGE,{"disambiguationData":[TD([[subQ2,-1.0]])],"derivedFrom":subQ1}),1.0]])]});}
            var Q239;
            {var subQ0=sQuery(id+"F0.wireOp",EDGE,"E20");var subQ1=sQuery(id+"F0.wireOp",EDGE,"E7");var subQ2=makeQuery(id+"F0.imprint","INTERSECT",VERTEX,{"derivedFrom":[subQ1,subQ0]});Q239=makeQuery(id+"F0.imprint","IMPRINT",FACE,{"disambiguationData":[TD([[makeQuery(id+"F0.imprint","IMPRINT",EDGE,{"disambiguationData":[TD([[subQ2,-1.0]])],"derivedFrom":subQ1}),1.0]])]});}
            var Q240;
            {var subQ0=sQuery(id+"F0.wireOp",EDGE,"E2");var subQ1=sQuery(id+"F0.wireOp",EDGE,"E0.top");var subQ2=makeQuery(id+"F0.imprint","INTERSECT",VERTEX,{"derivedFrom":[subQ1,subQ0]});Q240=makeQuery(id+"F0.imprint","IMPRINT",FACE,{"disambiguationData":[TD([[makeQuery(id+"F0.imprint","IMPRINT",EDGE,{"disambiguationData":[TD([[subQ2,-1.0]])],"derivedFrom":subQ1}),1.0]])]});}
            var Q241;
            {var subQ0=sQuery(id+"F0.wireOp",EDGE,"E28");var subQ1=sQuery(id+"F0.wireOp",EDGE,"E2");var subQ2=makeQuery(id+"F0.imprint","INTERSECT",VERTEX,{"derivedFrom":[subQ1,subQ0]});Q241=makeQuery(id+"F0.imprint","IMPRINT",FACE,{"disambiguationData":[TD([[makeQuery(id+"F0.imprint","IMPRINT",EDGE,{"disambiguationData":[TD([[subQ2,-1.0]])],"derivedFrom":subQ1}),1.0]])]});}
            var Q242;
            {var subQ0=sQuery(id+"F0.wireOp",EDGE,"E28");var subQ1=sQuery(id+"F0.wireOp",EDGE,"E5");var subQ2=makeQuery(id+"F0.imprint","INTERSECT",VERTEX,{"derivedFrom":[subQ1,subQ0]});Q242=makeQuery(id+"F0.imprint","IMPRINT",FACE,{"disambiguationData":[TD([[makeQuery(id+"F0.imprint","IMPRINT",EDGE,{"disambiguationData":[TD([[subQ2,-1.0]])],"derivedFrom":subQ1}),1.0]])]});}
            var Q243;
            {var subQ0=sQuery(id+"F0.wireOp",EDGE,"E34");var subQ1=sQuery(id+"F0.wireOp",EDGE,"E6");var subQ2=makeQuery(id+"F0.imprint","INTERSECT",VERTEX,{"derivedFrom":[subQ1,subQ0]});Q243=makeQuery(id+"F0.imprint","IMPRINT",FACE,{"disambiguationData":[TD([[makeQuery(id+"F0.imprint","IMPRINT",EDGE,{"disambiguationData":[TD([[subQ2,-1.0]])],"derivedFrom":subQ1}),1.0]])]});}
            var Q244;
            {var subQ0=sQuery(id+"F0.wireOp",EDGE,"E17");var subQ1=sQuery(id+"F0.wireOp",EDGE,"E0.top");var subQ2=makeQuery(id+"F0.imprint","INTERSECT",VERTEX,{"derivedFrom":[subQ1,subQ0]});Q244=makeQuery(id+"F0.imprint","IMPRINT",FACE,{"disambiguationData":[TD([[makeQuery(id+"F0.imprint","IMPRINT",EDGE,{"disambiguationData":[TD([[subQ2,-1.0]])],"derivedFrom":subQ1}),1.0]])]});}
            var Q245;
            {var subQ0=sQuery(id+"F0.wireOp",EDGE,"E21");var subQ1=sQuery(id+"F0.wireOp",EDGE,"E4");var subQ2=makeQuery(id+"F0.imprint","INTERSECT",VERTEX,{"derivedFrom":[subQ1,subQ0]});Q245=makeQuery(id+"F0.imprint","IMPRINT",FACE,{"disambiguationData":[TD([[makeQuery(id+"F0.imprint","IMPRINT",EDGE,{"disambiguationData":[TD([[subQ2,-1.0]])],"derivedFrom":subQ1}),1.0]])]});}
            var Q246;
            {var subQ0=sQuery(id+"F0.wireOp",EDGE,"E19");var subQ1=sQuery(id+"F0.wireOp",EDGE,"E0.right");var subQ2=makeQuery(id+"F0.imprint","INTERSECT",VERTEX,{"derivedFrom":[subQ1,subQ0]});Q246=makeQuery(id+"F0.imprint","IMPRINT",FACE,{"disambiguationData":[TD([[makeQuery(id+"F0.imprint","IMPRINT",EDGE,{"disambiguationData":[TD([[subQ2,-1.0]])],"derivedFrom":subQ1}),-1.0]])]});}
            var Q247;
            {var subQ0=sQuery(id+"F0.wireOp",EDGE,"E5");var subQ1=sQuery(id+"F0.wireOp",EDGE,"E0.top");var subQ2=makeQuery(id+"F0.imprint","INTERSECT",VERTEX,{"derivedFrom":[subQ1,subQ0]});Q247=makeQuery(id+"F0.imprint","IMPRINT",FACE,{"disambiguationData":[TD([[makeQuery(id+"F0.imprint","IMPRINT",EDGE,{"disambiguationData":[TD([[subQ2,-1.0]])],"derivedFrom":subQ1}),1.0]])]});}
            var Q248;
            {var subQ0=sQuery(id+"F0.wireOp",EDGE,"E26");var subQ1=sQuery(id+"F0.wireOp",EDGE,"E4");var subQ2=makeQuery(id+"F0.imprint","INTERSECT",VERTEX,{"derivedFrom":[subQ1,subQ0]});Q248=makeQuery(id+"F0.imprint","IMPRINT",FACE,{"disambiguationData":[TD([[makeQuery(id+"F0.imprint","IMPRINT",EDGE,{"disambiguationData":[TD([[subQ2,-1.0]])],"derivedFrom":subQ1}),1.0]])]});}
            var Q249;
            {var subQ0=sQuery(id+"F0.wireOp",EDGE,"E1");var subQ1=sQuery(id+"F0.wireOp",EDGE,"E0.bottom");var subQ2=makeQuery(id+"F0.imprint","INTERSECT",VERTEX,{"derivedFrom":[subQ1,subQ0]});Q249=makeQuery(id+"F0.imprint","IMPRINT",FACE,{"disambiguationData":[TD([[makeQuery(id+"F0.imprint","IMPRINT",EDGE,{"disambiguationData":[TD([[subQ2,-1.0]])],"derivedFrom":subQ1}),-1.0]])]});}
            var Q250;
            {var subQ0=sQuery(id+"F0.wireOp",EDGE,"E33");var subQ1=sQuery(id+"F0.wireOp",EDGE,"E4");var subQ2=makeQuery(id+"F0.imprint","INTERSECT",VERTEX,{"derivedFrom":[subQ1,subQ0]});Q250=makeQuery(id+"F0.imprint","IMPRINT",FACE,{"disambiguationData":[TD([[makeQuery(id+"F0.imprint","IMPRINT",EDGE,{"disambiguationData":[TD([[subQ2,-1.0]])],"derivedFrom":subQ1}),1.0]])]});}
            var Q251;
            {var subQ0=sQuery(id+"F0.wireOp",EDGE,"E19");var subQ1=sQuery(id+"F0.wireOp",EDGE,"E4");var subQ2=makeQuery(id+"F0.imprint","INTERSECT",VERTEX,{"derivedFrom":[subQ1,subQ0]});Q251=makeQuery(id+"F0.imprint","IMPRINT",FACE,{"disambiguationData":[TD([[makeQuery(id+"F0.imprint","IMPRINT",EDGE,{"disambiguationData":[TD([[subQ2,-1.0]])],"derivedFrom":subQ1}),1.0]])]});}
            var Q252;
            {var subQ0=sQuery(id+"F0.wireOp",EDGE,"E3");var subQ1=sQuery(id+"F0.wireOp",EDGE,"E0.top");var subQ2=makeQuery(id+"F0.imprint","INTERSECT",VERTEX,{"derivedFrom":[subQ1,subQ0]});Q252=makeQuery(id+"F0.imprint","IMPRINT",FACE,{"disambiguationData":[TD([[makeQuery(id+"F0.imprint","IMPRINT",EDGE,{"disambiguationData":[TD([[subQ2,-1.0]])],"derivedFrom":subQ1}),1.0]])]});}
            var Q253;
            {var subQ0=sQuery(id+"F0.wireOp",EDGE,"E28");var subQ1=sQuery(id+"F0.wireOp",EDGE,"E0.right");var subQ2=makeQuery(id+"F0.imprint","INTERSECT",VERTEX,{"derivedFrom":[subQ1,subQ0]});Q253=makeQuery(id+"F0.imprint","IMPRINT",FACE,{"disambiguationData":[TD([[makeQuery(id+"F0.imprint","IMPRINT",EDGE,{"disambiguationData":[TD([[subQ2,-1.0]])],"derivedFrom":subQ1}),-1.0]])]});}
            var Q254;
            {var subQ0=sQuery(id+"F0.wireOp",EDGE,"E23");var subQ1=sQuery(id+"F0.wireOp",EDGE,"E4");var subQ2=makeQuery(id+"F0.imprint","INTERSECT",VERTEX,{"derivedFrom":[subQ1,subQ0]});Q254=makeQuery(id+"F0.imprint","IMPRINT",FACE,{"disambiguationData":[TD([[makeQuery(id+"F0.imprint","IMPRINT",EDGE,{"disambiguationData":[TD([[subQ2,-1.0]])],"derivedFrom":subQ1}),1.0]])]});}
            var Q255;
            {var subQ0=sQuery(id+"F0.wireOp",EDGE,"E32");var subQ1=sQuery(id+"F0.wireOp",EDGE,"E0.right");var subQ2=makeQuery(id+"F0.imprint","INTERSECT",VERTEX,{"derivedFrom":[subQ1,subQ0]});Q255=makeQuery(id+"F0.imprint","IMPRINT",FACE,{"disambiguationData":[TD([[makeQuery(id+"F0.imprint","IMPRINT",EDGE,{"disambiguationData":[TD([[subQ2,-1.0]])],"derivedFrom":subQ1}),-1.0]])]});}
            var Q256;
            {var subQ0=sQuery(id+"F0.wireOp",EDGE,"E27");var subQ1=sQuery(id+"F0.wireOp",EDGE,"E0.right");var subQ2=makeQuery(id+"F0.imprint","INTERSECT",VERTEX,{"derivedFrom":[subQ1,subQ0]});Q256=makeQuery(id+"F0.imprint","IMPRINT",FACE,{"disambiguationData":[TD([[makeQuery(id+"F0.imprint","IMPRINT",EDGE,{"disambiguationData":[TD([[subQ2,-1.0]])],"derivedFrom":subQ1}),-1.0]])]});}
            var Q257;
            {var subQ0=sQuery(id+"F0.wireOp",EDGE,"E6");var subQ1=sQuery(id+"F0.wireOp",EDGE,"E0.top");var subQ2=makeQuery(id+"F0.imprint","INTERSECT",VERTEX,{"derivedFrom":[subQ1,subQ0]});Q257=makeQuery(id+"F0.imprint","IMPRINT",FACE,{"disambiguationData":[TD([[makeQuery(id+"F0.imprint","IMPRINT",EDGE,{"disambiguationData":[TD([[subQ2,-1.0]])],"derivedFrom":subQ1}),1.0]])]});}
            var Q258;
            {var subQ0=sQuery(id+"F0.wireOp",EDGE,"E20");var subQ1=sQuery(id+"F0.wireOp",EDGE,"E0.left");var subQ2=makeQuery(id+"F0.imprint","INTERSECT",VERTEX,{"derivedFrom":[subQ1,subQ0]});Q258=makeQuery(id+"F0.imprint","IMPRINT",FACE,{"disambiguationData":[TD([[makeQuery(id+"F0.imprint","IMPRINT",EDGE,{"disambiguationData":[TD([[subQ2,-1.0]])],"derivedFrom":subQ1}),1.0]])]});}
            var Q259;
            {var subQ0=sQuery(id+"F0.wireOp",EDGE,"E27");var subQ1=sQuery(id+"F0.wireOp",EDGE,"E0.left");var subQ2=makeQuery(id+"F0.imprint","INTERSECT",VERTEX,{"derivedFrom":[subQ1,subQ0]});Q259=makeQuery(id+"F0.imprint","IMPRINT",FACE,{"disambiguationData":[TD([[makeQuery(id+"F0.imprint","IMPRINT",EDGE,{"disambiguationData":[TD([[subQ2,-1.0]])],"derivedFrom":subQ1}),1.0]])]});}
            var Q260;
            {var subQ0=sQuery(id+"F0.wireOp",EDGE,"E34");var subQ1=sQuery(id+"F0.wireOp",EDGE,"E5");var subQ2=makeQuery(id+"F0.imprint","INTERSECT",VERTEX,{"derivedFrom":[subQ1,subQ0]});Q260=makeQuery(id+"F0.imprint","IMPRINT",FACE,{"disambiguationData":[TD([[makeQuery(id+"F0.imprint","IMPRINT",EDGE,{"disambiguationData":[TD([[subQ2,-1.0]])],"derivedFrom":subQ1}),1.0]])]});}
            var Q261;
            {var subQ0=sQuery(id+"F0.wireOp",EDGE,"E9");var subQ1=sQuery(id+"F0.wireOp",EDGE,"E0.bottom");var subQ2=makeQuery(id+"F0.imprint","INTERSECT",VERTEX,{"derivedFrom":[subQ1,subQ0]});Q261=makeQuery(id+"F0.imprint","IMPRINT",FACE,{"disambiguationData":[TD([[makeQuery(id+"F0.imprint","IMPRINT",EDGE,{"disambiguationData":[TD([[subQ2,-1.0]])],"derivedFrom":subQ1}),-1.0]])]});}
            var Q262;
            {var subQ0=sQuery(id+"F0.wireOp",EDGE,"E28");var subQ1=sQuery(id+"F0.wireOp",EDGE,"E14");var subQ2=makeQuery(id+"F0.imprint","INTERSECT",VERTEX,{"derivedFrom":[subQ1,subQ0]});Q262=makeQuery(id+"F0.imprint","IMPRINT",FACE,{"disambiguationData":[TD([[makeQuery(id+"F0.imprint","IMPRINT",EDGE,{"disambiguationData":[TD([[subQ2,-1.0]])],"derivedFrom":subQ1}),1.0]])]});}
            var Q263;
            {var subQ0=sQuery(id+"F0.wireOp",EDGE,"E34");var subQ1=sQuery(id+"F0.wireOp",EDGE,"E0.right");var subQ2=makeQuery(id+"F0.imprint","INTERSECT",VERTEX,{"derivedFrom":[subQ1,subQ0]});Q263=makeQuery(id+"F0.imprint","IMPRINT",FACE,{"disambiguationData":[TD([[makeQuery(id+"F0.imprint","IMPRINT",EDGE,{"disambiguationData":[TD([[subQ2,-1.0]])],"derivedFrom":subQ1}),-1.0]])]});}
            var Q264;
            {var subQ0=sQuery(id+"F0.wireOp",EDGE,"E28");var subQ1=sQuery(id+"F0.wireOp",EDGE,"E16");var subQ2=makeQuery(id+"F0.imprint","INTERSECT",VERTEX,{"derivedFrom":[subQ1,subQ0]});Q264=makeQuery(id+"F0.imprint","IMPRINT",FACE,{"disambiguationData":[TD([[makeQuery(id+"F0.imprint","IMPRINT",EDGE,{"disambiguationData":[TD([[subQ2,-1.0]])],"derivedFrom":subQ1}),1.0]])]});}
            var Q265;
            {var subQ0=sQuery(id+"F0.wireOp",EDGE,"E24");var subQ1=sQuery(id+"F0.wireOp",EDGE,"E0.right");var subQ2=makeQuery(id+"F0.imprint","INTERSECT",VERTEX,{"derivedFrom":[subQ1,subQ0]});Q265=makeQuery(id+"F0.imprint","IMPRINT",FACE,{"disambiguationData":[TD([[makeQuery(id+"F0.imprint","IMPRINT",EDGE,{"disambiguationData":[TD([[subQ2,-1.0]])],"derivedFrom":subQ1}),-1.0]])]});}
            var Q266;
            {var subQ0=sQuery(id+"F0.wireOp",EDGE,"E20");var subQ1=sQuery(id+"F0.wireOp",EDGE,"E13");var subQ2=makeQuery(id+"F0.imprint","INTERSECT",VERTEX,{"derivedFrom":[subQ1,subQ0]});Q266=makeQuery(id+"F0.imprint","IMPRINT",FACE,{"disambiguationData":[TD([[makeQuery(id+"F0.imprint","IMPRINT",EDGE,{"disambiguationData":[TD([[subQ2,-1.0]])],"derivedFrom":subQ1}),1.0]])]});}
            var Q267;
            {var subQ0=sQuery(id+"F0.wireOp",EDGE,"E20");var subQ1=sQuery(id+"F0.wireOp",EDGE,"E12");var subQ2=makeQuery(id+"F0.imprint","INTERSECT",VERTEX,{"derivedFrom":[subQ1,subQ0]});Q267=makeQuery(id+"F0.imprint","IMPRINT",FACE,{"disambiguationData":[TD([[makeQuery(id+"F0.imprint","IMPRINT",EDGE,{"disambiguationData":[TD([[subQ2,-1.0]])],"derivedFrom":subQ1}),1.0]])]});}
            var Q268;
            {var subQ0=sQuery(id+"F0.wireOp",EDGE,"E12");var subQ1=sQuery(id+"F0.wireOp",EDGE,"E0.bottom");var subQ2=makeQuery(id+"F0.imprint","INTERSECT",VERTEX,{"derivedFrom":[subQ1,subQ0]});Q268=makeQuery(id+"F0.imprint","IMPRINT",FACE,{"disambiguationData":[TD([[makeQuery(id+"F0.imprint","IMPRINT",EDGE,{"disambiguationData":[TD([[subQ2,-1.0]])],"derivedFrom":subQ1}),-1.0]])]});}
            var Q269;
            {var subQ0=sQuery(id+"F0.wireOp",EDGE,"E6");var subQ1=sQuery(id+"F0.wireOp",EDGE,"E0.bottom");var subQ2=makeQuery(id+"F0.imprint","INTERSECT",VERTEX,{"derivedFrom":[subQ1,subQ0]});Q269=makeQuery(id+"F0.imprint","IMPRINT",FACE,{"disambiguationData":[TD([[makeQuery(id+"F0.imprint","IMPRINT",EDGE,{"disambiguationData":[TD([[subQ2,-1.0]])],"derivedFrom":subQ1}),-1.0]])]});}
            var Q270;
            {var subQ0=sQuery(id+"F0.wireOp",EDGE,"E10");var subQ1=sQuery(id+"F0.wireOp",EDGE,"E0.bottom");var subQ2=makeQuery(id+"F0.imprint","INTERSECT",VERTEX,{"derivedFrom":[subQ1,subQ0]});Q270=makeQuery(id+"F0.imprint","IMPRINT",FACE,{"disambiguationData":[TD([[makeQuery(id+"F0.imprint","IMPRINT",EDGE,{"disambiguationData":[TD([[subQ2,-1.0]])],"derivedFrom":subQ1}),-1.0]])]});}
            var Q271;
            {var subQ0=sQuery(id+"F0.wireOp",EDGE,"E34");var subQ1=sQuery(id+"F0.wireOp",EDGE,"E3");var subQ2=makeQuery(id+"F0.imprint","INTERSECT",VERTEX,{"derivedFrom":[subQ1,subQ0]});Q271=makeQuery(id+"F0.imprint","IMPRINT",FACE,{"disambiguationData":[TD([[makeQuery(id+"F0.imprint","IMPRINT",EDGE,{"disambiguationData":[TD([[subQ2,-1.0]])],"derivedFrom":subQ1}),1.0]])]});}
            var Q272;
            {var subQ0=sQuery(id+"F0.wireOp",EDGE,"E15");var subQ1=sQuery(id+"F0.wireOp",EDGE,"E0.top");var subQ2=makeQuery(id+"F0.imprint","INTERSECT",VERTEX,{"derivedFrom":[subQ1,subQ0]});Q272=makeQuery(id+"F0.imprint","IMPRINT",FACE,{"disambiguationData":[TD([[makeQuery(id+"F0.imprint","IMPRINT",EDGE,{"disambiguationData":[TD([[subQ2,-1.0]])],"derivedFrom":subQ1}),1.0]])]});}
            var Q273;
            {var subQ0=sQuery(id+"F0.wireOp",EDGE,"E28");var subQ1=sQuery(id+"F0.wireOp",EDGE,"E4");var subQ2=makeQuery(id+"F0.imprint","INTERSECT",VERTEX,{"derivedFrom":[subQ1,subQ0]});Q273=makeQuery(id+"F0.imprint","IMPRINT",FACE,{"disambiguationData":[TD([[makeQuery(id+"F0.imprint","IMPRINT",EDGE,{"disambiguationData":[TD([[subQ2,-1.0]])],"derivedFrom":subQ1}),1.0]])]});}
            var Q274;
            {var subQ0=sQuery(id+"F0.wireOp",EDGE,"E25");var subQ1=sQuery(id+"F0.wireOp",EDGE,"E0.right");var subQ2=makeQuery(id+"F0.imprint","INTERSECT",VERTEX,{"derivedFrom":[subQ1,subQ0]});Q274=makeQuery(id+"F0.imprint","IMPRINT",FACE,{"disambiguationData":[TD([[makeQuery(id+"F0.imprint","IMPRINT",EDGE,{"disambiguationData":[TD([[subQ2,-1.0]])],"derivedFrom":subQ1}),-1.0]])]});}
            var Q275;
            {var subQ0=sQuery(id+"F0.wireOp",EDGE,"E34");var subQ1=sQuery(id+"F0.wireOp",EDGE,"E4");var subQ2=makeQuery(id+"F0.imprint","INTERSECT",VERTEX,{"derivedFrom":[subQ1,subQ0]});Q275=makeQuery(id+"F0.imprint","IMPRINT",FACE,{"disambiguationData":[TD([[makeQuery(id+"F0.imprint","IMPRINT",EDGE,{"disambiguationData":[TD([[subQ2,-1.0]])],"derivedFrom":subQ1}),1.0]])]});}
            var Q276;
            {var subQ0=sQuery(id+"F0.wireOp",EDGE,"E0.right");var subQ1=sQuery(id+"F0.wireOp",EDGE,"E0.top");var subQ2=makeQuery(id+"F0.imprint","INTERSECT",VERTEX,{"derivedFrom":[subQ1,subQ0]});Q276=makeQuery(id+"F0.imprint","IMPRINT",FACE,{"disambiguationData":[TD([[makeQuery(id+"F0.imprint","IMPRINT",EDGE,{"disambiguationData":[TD([[subQ2,1.0]])],"derivedFrom":subQ1}),1.0]])]});}
            var Q277;
            {var subQ0=sQuery(id+"F0.wireOp",EDGE,"E0.right");var subQ1=sQuery(id+"F0.wireOp",EDGE,"E0.bottom");var subQ2=makeQuery(id+"F0.imprint","INTERSECT",VERTEX,{"derivedFrom":[subQ1,subQ0]});Q277=makeQuery(id+"F0.imprint","IMPRINT",FACE,{"disambiguationData":[TD([[makeQuery(id+"F0.imprint","IMPRINT",EDGE,{"disambiguationData":[TD([[subQ2,1.0]])],"derivedFrom":subQ1}),-1.0]])]});}
            var Q278;
            {var subQ0=sQuery(id+"F0.wireOp",EDGE,"E0.left");var subQ1=sQuery(id+"F0.wireOp",EDGE,"E0.top");var subQ2=makeQuery(id+"F0.imprint","INTERSECT",VERTEX,{"derivedFrom":[subQ1,subQ0]});Q278=makeQuery(id+"F0.imprint","IMPRINT",FACE,{"disambiguationData":[TD([[makeQuery(id+"F0.imprint","IMPRINT",EDGE,{"disambiguationData":[TD([[subQ2,-1.0]])],"derivedFrom":subQ1}),1.0]])]});}
            var Q279;
            {var subQ0=sQuery(id+"F0.wireOp",EDGE,"E0.left");var subQ1=sQuery(id+"F0.wireOp",EDGE,"E0.bottom");var subQ2=makeQuery(id+"F0.imprint","INTERSECT",VERTEX,{"derivedFrom":[subQ1,subQ0]});Q279=makeQuery(id+"F0.imprint","IMPRINT",FACE,{"disambiguationData":[TD([[makeQuery(id+"F0.imprint","IMPRINT",EDGE,{"disambiguationData":[TD([[subQ2,-1.0]])],"derivedFrom":subQ1}),-1.0]])]});}
            extrude(context, id + "F1", {"entities" : qUnion([Q0, Q1, Q2, Q3, Q4, Q5, Q6, Q7, Q8, Q9, Q10, Q11, Q12, Q13, Q14, Q15, Q16, Q17, Q18, Q19, Q20, Q21, Q22, Q23, Q24, Q25, Q26, Q27, Q28, Q29, Q30, Q31, Q32, Q33, Q34, Q35, Q36, Q37, Q38, Q39, Q40, Q41, Q42, Q43, Q44, Q45, Q46, Q47, Q48, Q49, Q50, Q51, Q52, Q53, Q54, Q55, Q56, Q57, Q58, Q59, Q60, Q61, Q62, Q63, Q64, Q65, Q66, Q67, Q68, Q69, Q70, Q71, Q72, Q73, Q74, Q75, Q76, Q77, Q78, Q79, Q80, Q81, Q82, Q83, Q84, Q85, Q86, Q87, Q88, Q89, Q90, Q91, Q92, Q93, Q94, Q95, Q96, Q97, Q98, Q99, Q100, Q101, Q102, Q103, Q104, Q105, Q106, Q107, Q108, Q109, Q110, Q111, Q112, Q113, Q114, Q115, Q116, Q117, Q118, Q119, Q120, Q121, Q122, Q123, Q124, Q125, Q126, Q127, Q128, Q129, Q130, Q131, Q132, Q133, Q134, Q135, Q136, Q137, Q138, Q139, Q140, Q141, Q142, Q143, Q144, Q145, Q146, Q147, Q148, Q149, Q150, Q151, Q152, Q153, Q154, Q155, Q156, Q157, Q158, Q159, Q160, Q161, Q162, Q163, Q164, Q165, Q166, Q167, Q168, Q169, Q170, Q171, Q172, Q173, Q174, Q175, Q176, Q177, Q178, Q179, Q180, Q181, Q182, Q183, Q184, Q185, Q186, Q187, Q188, Q189, Q190, Q191, Q192, Q193, Q194, Q195, Q196, Q197, Q198, Q199, Q200, Q201, Q202, Q203, Q204, Q205, Q206, Q207, Q208, Q209, Q210, Q211, Q212, Q213, Q214, Q215, Q216, Q217, Q218, Q219, Q220, Q221, Q222, Q223, Q224, Q225, Q226, Q227, Q228, Q229, Q230, Q231, Q232, Q233, Q234, Q235, Q236, Q237, Q238, Q239, Q240, Q241, Q242, Q243, Q244, Q245, Q246, Q247, Q248, Q249, Q250, Q251, Q252, Q253, Q254, Q255, Q256, Q257, Q258, Q259, Q260, Q261, Q262, Q263, Q264, Q265, Q266, Q267, Q268, Q269, Q270, Q271, Q272, Q273, Q274, Q275, Q276, Q277, Q278, Q279]), "depth" : 1 * mm, "offsetDistance" : 25 * mm});
        }
        {
            var Q0;
            Q0=makeQuery(id+"F1.opExtrude","SWEPT_FACE",FACE,{"disambiguationData":[OSD([sQuery(id+"F0.wireOp",EDGE,"E0.left")])]});
            var Q1;
            Q1=makeQuery(id+"F1.opExtrude","SWEPT_FACE",FACE,{"disambiguationData":[OSD([sQuery(id+"F0.wireOp",EDGE,"E0.top")])]});
            var Q2;
            Q2=makeQuery(id+"F1.opExtrude","SWEPT_FACE",FACE,{"disambiguationData":[OSD([sQuery(id+"F0.wireOp",EDGE,"E0.right")])]});
            var Q3;
            Q3=makeQuery(id+"F1.opExtrude","SWEPT_FACE",FACE,{"disambiguationData":[OSD([sQuery(id+"F0.wireOp",EDGE,"E0.bottom")])]});
            fillet(context, id + "F2", {"entities" : qUnion([Q0, Q1, Q2, Q3]), "radius" : 0.1 * mm, "tangentPropagation" : true, "allowEdgeOverflow" : false});
        }
    });
